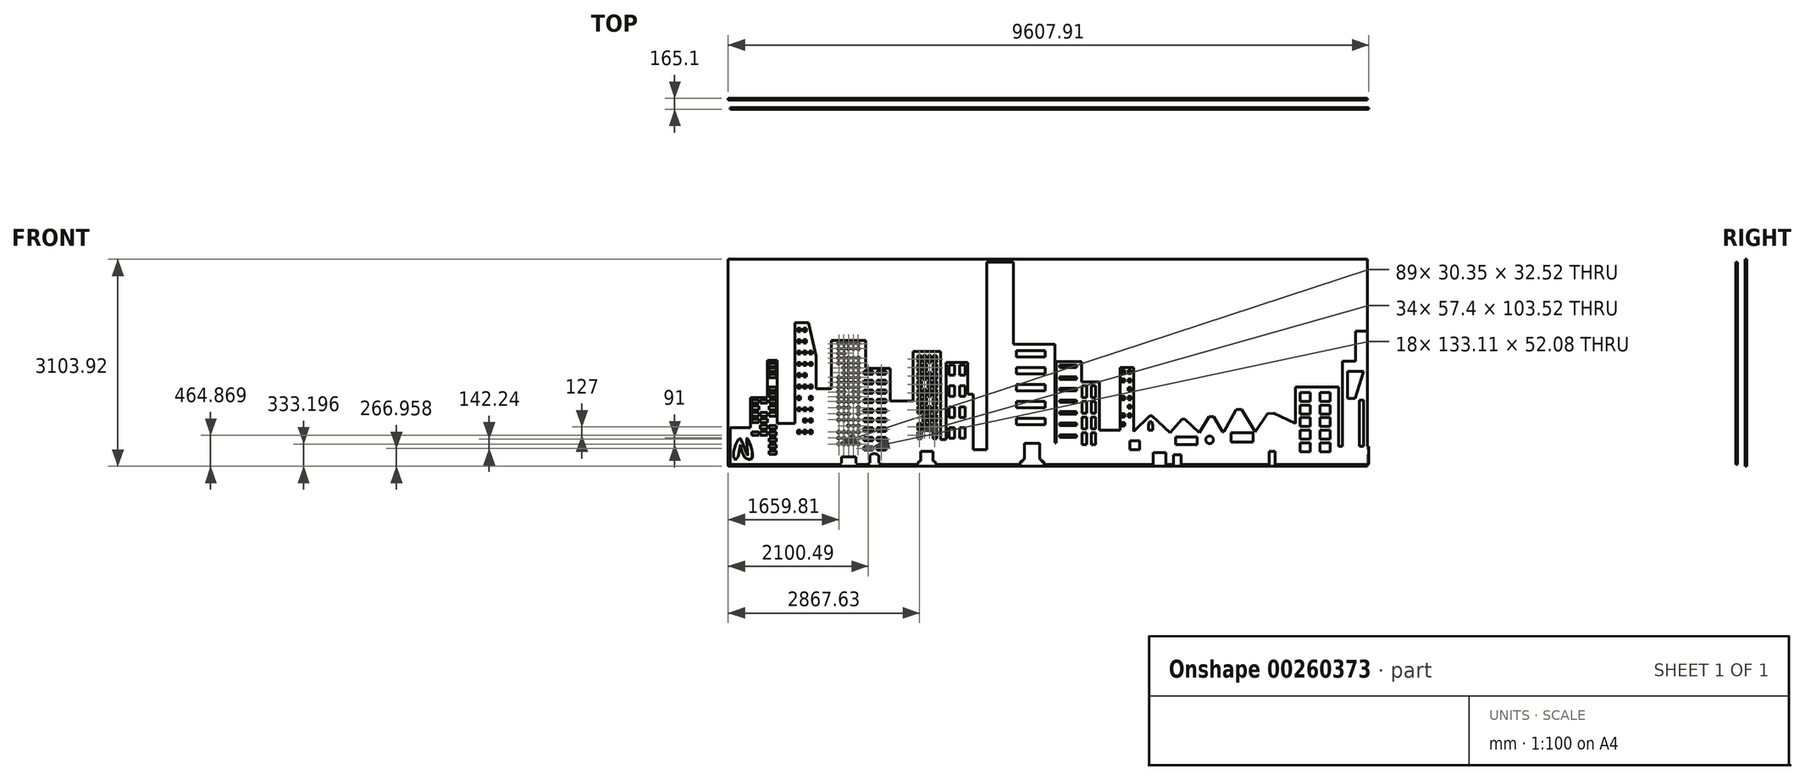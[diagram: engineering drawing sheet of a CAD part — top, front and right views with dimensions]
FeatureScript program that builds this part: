
annotation { "Feature Type Name" : "Feature", "Feature Type Description" : "" }
export const myFeature = defineFeature(function(context is Context, id is Id, definition is map)
    precondition{}
    {
        {
            var Q0;
            Q0=qCreatedBy(makeId("Front.planeOp"),FACE);
            var sketch = newSketch(context, id + "F0", { "sketchPlane" : qUnion([Q0])});
            skLineSegment(sketch, "E0.top", {"start": v(-4050, -823.15) * mm, "end": v(200, -823.15) * mm});
            skLineSegment(sketch, "E0.right", {"start": v(5530, -547.29) * mm, "end": v(5530, -823.15) * mm});
            skLineSegment(sketch, "E1", {"start": v(0, 692.97) * mm, "end": v(0, 1385.94) * mm, "construction": true});
            skLineSegment(sketch, "E2.bottom", {"start": v(-200, -823.15) * mm, "end": v(200, -823.15) * mm});
            skLineSegment(sketch, "E2.top", {"start": v(-200, 2209.1) * mm, "end": v(200, 2209.1) * mm});
            skPoint(sketch, "E2.middle", {"position": v(0, 692.97) * mm});
            skLineSegment(sketch, "E3", {"start": v(-4050, -267.9) * mm, "end": v(-3744.51, -267.9) * mm});
            skLineSegment(sketch, "E4", {"start": v(-3744.51, -267.9) * mm, "end": v(-3744.51, 182.25) * mm});
            skLineSegment(sketch, "E5", {"start": v(-3744.51, 182.25) * mm, "end": v(-3487.34, 182.25) * mm});
            skLineSegment(sketch, "E6", {"start": v(-2077.34, -479.2) * mm, "end": v(-2077.34, 617.88) * mm});
            skLineSegment(sketch, "E7", {"start": v(-2077.34, 617.88) * mm, "end": v(-1645.57, 617.88) * mm});
            skLineSegment(sketch, "E8", {"start": v(-1645.57, 617.88) * mm, "end": v(-1645.57, 127.13) * mm});
            skLineSegment(sketch, "E9", {"start": v(-1645.57, 127.13) * mm, "end": v(-1305.66, 127.13) * mm});
            skLineSegment(sketch, "E10", {"start": v(-1305.66, 127.13) * mm, "end": v(-1305.66, 871.24) * mm});
            skLineSegment(sketch, "E11", {"start": v(-1305.66, 871.24) * mm, "end": v(-892.27, 871.24) * mm});
            skLineSegment(sketch, "E12", {"start": v(-892.27, 871.24) * mm, "end": v(-892.27, -451.63) * mm});
            skLineSegment(sketch, "E13", {"start": v(-892.27, -451.63) * mm, "end": v(-812.32, -451.63) * mm});
            skLineSegment(sketch, "E14", {"start": v(-484.42, 228.18) * mm, "end": v(-402.68, 228.18) * mm});
            skLineSegment(sketch, "E15", {"start": v(-402.68, 228.18) * mm, "end": v(-402.68, -598.62) * mm});
            skLineSegment(sketch, "E16", {"start": v(-402.68, -598.62) * mm, "end": v(-200, -598.62) * mm});
            skLineSegment(sketch, "E17.right", {"start": v(677.5, 629.06) * mm, "end": v(677.5, 534.62) * mm});
            skLineSegment(sketch, "E18", {"start": v(-812.32, 709.79) * mm, "end": v(-484.42, 709.79) * mm});
            skLineSegment(sketch, "E19", {"start": v(-484.42, 709.79) * mm, "end": v(-484.42, 228.18) * mm});
            skLineSegment(sketch, "E20", {"start": v(840.6, 718.46) * mm, "end": v(1218.73, 718.46) * mm});
            skLineSegment(sketch, "E21", {"start": v(1218.73, 718.46) * mm, "end": v(1218.73, 413.8) * mm});
            skLineSegment(sketch, "E22", {"start": v(2725.07, -144.63) * mm, "end": v(2549.54, -345.87) * mm});
            skLineSegment(sketch, "E23", {"start": v(2768.68, -144.63) * mm, "end": v(2987.94, -346.12) * mm});
            skLineSegment(sketch, "E24", {"start": v(2486.2, -646.21) * mm, "end": v(2486.2, -823.15) * mm});
            skLineSegment(sketch, "E25", {"start": v(1218.73, 413.8) * mm, "end": v(1485.88, 413.8) * mm});
            skLineSegment(sketch, "E26", {"start": v(1485.88, 413.8) * mm, "end": v(1485.88, -308) * mm});
            skLineSegment(sketch, "E27", {"start": v(1485.88, -308) * mm, "end": v(1796.4, -308) * mm});
            skLineSegment(sketch, "E28", {"start": v(1796.4, -308) * mm, "end": v(1796.4, 630.35) * mm});
            skLineSegment(sketch, "E29", {"start": v(1796.4, 630.35) * mm, "end": v(2001.46, 630.35) * mm});
            skLineSegment(sketch, "E30", {"start": v(2001.46, 630.35) * mm, "end": v(2001.46, -329.92) * mm});
            skPoint(sketch, "E31.orphan", {"position": v(2356.52, -567.16) * mm});
            skLineSegment(sketch, "E32", {"start": v(2001.46, -329.92) * mm, "end": v(2244.2, -90.17) * mm});
            skLineSegment(sketch, "E33", {"start": v(2923.06, 0) * mm, "end": v(2923.06, 0) * mm});
            skLineSegment(sketch, "E34.2.0.0", {"start": v(-2433.27, 103.48) * mm, "end": v(-2402.92, 103.48) * mm});
            skLineSegment(sketch, "E34.2.0.1", {"start": v(-2402.92, 136) * mm, "end": v(-2402.92, 103.48) * mm});
            skLineSegment(sketch, "E34.2.0.2", {"start": v(-2433.27, 136) * mm, "end": v(-2402.92, 136) * mm});
            skLineSegment(sketch, "E34.2.0.3", {"start": v(-2433.27, 136) * mm, "end": v(-2433.27, 103.48) * mm});
            skLineSegment(sketch, "E35.bottom", {"start": v(-2043.97, 580.46) * mm, "end": v(-1910.86, 580.46) * mm});
            skLineSegment(sketch, "E35.top", {"start": v(-2043.97, 528.38) * mm, "end": v(-1910.86, 528.38) * mm});
            skLineSegment(sketch, "E35.left", {"start": v(-2043.97, 580.46) * mm, "end": v(-2043.97, 528.38) * mm});
            skLineSegment(sketch, "E35.right", {"start": v(-1910.86, 580.46) * mm, "end": v(-1910.86, 528.38) * mm});
            skLineSegment(sketch, "E36.0.1.0", {"start": v(-2043.97, 438.22) * mm, "end": v(-1910.86, 438.22) * mm});
            skLineSegment(sketch, "E36.0.1.1", {"start": v(-2043.97, 386.14) * mm, "end": v(-1910.86, 386.14) * mm});
            skLineSegment(sketch, "E36.0.1.2", {"start": v(-1910.86, 438.22) * mm, "end": v(-1910.86, 386.14) * mm});
            skLineSegment(sketch, "E36.0.1.3", {"start": v(-2043.97, 438.22) * mm, "end": v(-2043.97, 386.14) * mm});
            skLineSegment(sketch, "E36.0.2.0", {"start": v(-2043.97, 295.98) * mm, "end": v(-1910.86, 295.98) * mm});
            skLineSegment(sketch, "E36.0.2.1", {"start": v(-2043.97, 243.9) * mm, "end": v(-1910.86, 243.9) * mm});
            skLineSegment(sketch, "E36.0.2.2", {"start": v(-1910.86, 295.98) * mm, "end": v(-1910.86, 243.9) * mm});
            skLineSegment(sketch, "E36.0.2.3", {"start": v(-2043.97, 295.98) * mm, "end": v(-2043.97, 243.9) * mm});
            skLineSegment(sketch, "E36.0.3.0", {"start": v(-2043.97, 153.74) * mm, "end": v(-1910.86, 153.74) * mm});
            skLineSegment(sketch, "E36.0.3.1", {"start": v(-2043.97, 101.66) * mm, "end": v(-1910.86, 101.66) * mm});
            skLineSegment(sketch, "E36.0.3.2", {"start": v(-1910.86, 153.74) * mm, "end": v(-1910.86, 101.66) * mm});
            skLineSegment(sketch, "E36.0.3.3", {"start": v(-2043.97, 153.74) * mm, "end": v(-2043.97, 101.66) * mm});
            skLineSegment(sketch, "E36.0.4.0", {"start": v(-2043.97, 11.5) * mm, "end": v(-1910.86, 11.5) * mm});
            skLineSegment(sketch, "E36.0.4.1", {"start": v(-2043.97, -40.58) * mm, "end": v(-1910.86, -40.58) * mm});
            skLineSegment(sketch, "E36.0.4.2", {"start": v(-1910.86, 11.5) * mm, "end": v(-1910.86, -40.58) * mm});
            skLineSegment(sketch, "E36.0.4.3", {"start": v(-2043.97, 11.5) * mm, "end": v(-2043.97, -40.58) * mm});
            skLineSegment(sketch, "E36.0.5.0", {"start": v(-2043.97, -130.74) * mm, "end": v(-1910.86, -130.74) * mm});
            skLineSegment(sketch, "E36.0.5.1", {"start": v(-2043.97, -182.82) * mm, "end": v(-1910.86, -182.82) * mm});
            skLineSegment(sketch, "E36.0.5.2", {"start": v(-1910.86, -130.74) * mm, "end": v(-1910.86, -182.82) * mm});
            skLineSegment(sketch, "E36.0.5.3", {"start": v(-2043.97, -130.74) * mm, "end": v(-2043.97, -182.82) * mm});
            skLineSegment(sketch, "E36.0.6.0", {"start": v(-2043.97, -272.98) * mm, "end": v(-1910.86, -272.98) * mm});
            skLineSegment(sketch, "E36.0.6.1", {"start": v(-2043.97, -325.06) * mm, "end": v(-1910.86, -325.06) * mm});
            skLineSegment(sketch, "E36.0.6.2", {"start": v(-1910.86, -272.98) * mm, "end": v(-1910.86, -325.06) * mm});
            skLineSegment(sketch, "E36.0.6.3", {"start": v(-2043.97, -272.98) * mm, "end": v(-2043.97, -325.06) * mm});
            skLineSegment(sketch, "E36.0.7.0", {"start": v(-2043.97, -415.22) * mm, "end": v(-1910.86, -415.22) * mm});
            skLineSegment(sketch, "E36.0.7.1", {"start": v(-2043.97, -467.3) * mm, "end": v(-1910.86, -467.3) * mm});
            skLineSegment(sketch, "E36.0.7.2", {"start": v(-1910.86, -415.22) * mm, "end": v(-1910.86, -467.3) * mm});
            skLineSegment(sketch, "E36.0.7.3", {"start": v(-2043.97, -415.22) * mm, "end": v(-2043.97, -467.3) * mm});
            skLineSegment(sketch, "E36.0.8.0", {"start": v(-2043.97, -557.46) * mm, "end": v(-1910.86, -557.46) * mm});
            skLineSegment(sketch, "E36.0.8.1", {"start": v(-2043.97, -609.54) * mm, "end": v(-1910.86, -609.54) * mm});
            skLineSegment(sketch, "E36.0.8.2", {"start": v(-1910.86, -557.46) * mm, "end": v(-1910.86, -609.54) * mm});
            skLineSegment(sketch, "E36.0.8.3", {"start": v(-2043.97, -557.46) * mm, "end": v(-2043.97, -609.54) * mm});
            skLineSegment(sketch, "E36.1.0.0", {"start": v(-1845.85, 580.46) * mm, "end": v(-1712.74, 580.46) * mm});
            skLineSegment(sketch, "E36.1.0.1", {"start": v(-1845.85, 528.38) * mm, "end": v(-1712.74, 528.38) * mm});
            skLineSegment(sketch, "E36.1.0.2", {"start": v(-1712.74, 580.46) * mm, "end": v(-1712.74, 528.38) * mm});
            skLineSegment(sketch, "E36.1.0.3", {"start": v(-1845.85, 580.46) * mm, "end": v(-1845.85, 528.38) * mm});
            skLineSegment(sketch, "E36.1.1.0", {"start": v(-1845.85, 438.22) * mm, "end": v(-1712.74, 438.22) * mm});
            skLineSegment(sketch, "E36.1.1.1", {"start": v(-1845.85, 386.14) * mm, "end": v(-1712.74, 386.14) * mm});
            skLineSegment(sketch, "E36.1.1.2", {"start": v(-1712.74, 438.22) * mm, "end": v(-1712.74, 386.14) * mm});
            skLineSegment(sketch, "E36.1.1.3", {"start": v(-1845.85, 438.22) * mm, "end": v(-1845.85, 386.14) * mm});
            skLineSegment(sketch, "E36.1.2.0", {"start": v(-1845.85, 295.98) * mm, "end": v(-1712.74, 295.98) * mm});
            skLineSegment(sketch, "E36.1.2.1", {"start": v(-1845.85, 243.9) * mm, "end": v(-1712.74, 243.9) * mm});
            skLineSegment(sketch, "E36.1.2.2", {"start": v(-1712.74, 295.98) * mm, "end": v(-1712.74, 243.9) * mm});
            skLineSegment(sketch, "E36.1.2.3", {"start": v(-1845.85, 295.98) * mm, "end": v(-1845.85, 243.9) * mm});
            skLineSegment(sketch, "E36.1.3.0", {"start": v(-1845.85, 153.74) * mm, "end": v(-1712.74, 153.74) * mm});
            skLineSegment(sketch, "E36.1.3.1", {"start": v(-1845.85, 101.66) * mm, "end": v(-1712.74, 101.66) * mm});
            skLineSegment(sketch, "E36.1.3.2", {"start": v(-1712.74, 153.74) * mm, "end": v(-1712.74, 101.66) * mm});
            skLineSegment(sketch, "E36.1.3.3", {"start": v(-1845.85, 153.74) * mm, "end": v(-1845.85, 101.66) * mm});
            skLineSegment(sketch, "E36.1.4.0", {"start": v(-1845.85, 11.5) * mm, "end": v(-1712.74, 11.5) * mm});
            skLineSegment(sketch, "E36.1.4.1", {"start": v(-1845.85, -40.58) * mm, "end": v(-1712.74, -40.58) * mm});
            skLineSegment(sketch, "E36.1.4.2", {"start": v(-1712.74, 11.5) * mm, "end": v(-1712.74, -40.58) * mm});
            skLineSegment(sketch, "E36.1.4.3", {"start": v(-1845.85, 11.5) * mm, "end": v(-1845.85, -40.58) * mm});
            skLineSegment(sketch, "E36.1.5.0", {"start": v(-1845.85, -130.74) * mm, "end": v(-1712.74, -130.74) * mm});
            skLineSegment(sketch, "E36.1.5.1", {"start": v(-1845.85, -182.82) * mm, "end": v(-1712.74, -182.82) * mm});
            skLineSegment(sketch, "E36.1.5.2", {"start": v(-1712.74, -130.74) * mm, "end": v(-1712.74, -182.82) * mm});
            skLineSegment(sketch, "E36.1.5.3", {"start": v(-1845.85, -130.74) * mm, "end": v(-1845.85, -182.82) * mm});
            skLineSegment(sketch, "E36.1.6.0", {"start": v(-1845.85, -272.98) * mm, "end": v(-1712.74, -272.98) * mm});
            skLineSegment(sketch, "E36.1.6.1", {"start": v(-1845.85, -325.06) * mm, "end": v(-1712.74, -325.06) * mm});
            skLineSegment(sketch, "E36.1.6.2", {"start": v(-1712.74, -272.98) * mm, "end": v(-1712.74, -325.06) * mm});
            skLineSegment(sketch, "E36.1.6.3", {"start": v(-1845.85, -272.98) * mm, "end": v(-1845.85, -325.06) * mm});
            skLineSegment(sketch, "E36.1.7.0", {"start": v(-1845.85, -415.22) * mm, "end": v(-1712.74, -415.22) * mm});
            skLineSegment(sketch, "E36.1.7.1", {"start": v(-1845.85, -467.3) * mm, "end": v(-1712.74, -467.3) * mm});
            skLineSegment(sketch, "E36.1.7.2", {"start": v(-1712.74, -415.22) * mm, "end": v(-1712.74, -467.3) * mm});
            skLineSegment(sketch, "E36.1.7.3", {"start": v(-1845.85, -415.22) * mm, "end": v(-1845.85, -467.3) * mm});
            skLineSegment(sketch, "E36.1.8.0", {"start": v(-1845.85, -557.46) * mm, "end": v(-1712.74, -557.46) * mm});
            skLineSegment(sketch, "E36.1.8.1", {"start": v(-1845.85, -609.54) * mm, "end": v(-1712.74, -609.54) * mm});
            skLineSegment(sketch, "E36.1.8.2", {"start": v(-1712.74, -557.46) * mm, "end": v(-1712.74, -609.54) * mm});
            skLineSegment(sketch, "E36.1.8.3", {"start": v(-1845.85, -557.46) * mm, "end": v(-1845.85, -609.54) * mm});
            skLineSegment(sketch, "E36.direction1", {"start": v(-2043.97, 580.46) * mm, "end": v(-1845.85, 580.46) * mm, "construction": true});
            skLineSegment(sketch, "E36.direction2", {"start": v(-2043.97, 580.46) * mm, "end": v(-2043.97, 438.22) * mm, "construction": true});
            skPoint(sketch, "E37.orphan", {"position": v(-2123.27, 617.88) * mm});
            skLineSegment(sketch, "E38", {"start": v(-2016.7, 617.88) * mm, "end": v(-2016.7, 1037.73) * mm});
            skLineSegment(sketch, "E39", {"start": v(-812.32, 709.79) * mm, "end": v(-812.32, -451.63) * mm});
            skLineSegment(sketch, "E40", {"start": v(200, 981.37) * mm, "end": v(819.93, 981.37) * mm});
            skLineSegment(sketch, "E41", {"start": v(819.93, 981.37) * mm, "end": v(819.93, 718.46) * mm});
            skPoint(sketch, "E42.orphan", {"position": v(0, 0) * mm});
            skPoint(sketch, "E43.orphan", {"position": v(819.93, 692.97) * mm});
            skPoint(sketch, "E44.end.orphan", {"position": v(-2100.3, 617.88) * mm});
            skLineSegment(sketch, "E45.bottom", {"start": v(-1238.98, 809.17) * mm, "end": v(-1181.58, 809.17) * mm});
            skLineSegment(sketch, "E45.top", {"start": v(-1238.98, 705.65) * mm, "end": v(-1181.58, 705.65) * mm});
            skLineSegment(sketch, "E45.left", {"start": v(-1238.98, 809.17) * mm, "end": v(-1238.98, 705.65) * mm});
            skLineSegment(sketch, "E45.right", {"start": v(-1181.58, 809.17) * mm, "end": v(-1181.58, 705.65) * mm});
            skLineSegment(sketch, "E46.0.1.0", {"start": v(-1238.98, 682.17) * mm, "end": v(-1238.98, 578.65) * mm});
            skLineSegment(sketch, "E46.0.1.1", {"start": v(-1181.58, 682.17) * mm, "end": v(-1181.58, 578.65) * mm});
            skLineSegment(sketch, "E46.0.1.2", {"start": v(-1238.98, 682.17) * mm, "end": v(-1181.58, 682.17) * mm});
            skLineSegment(sketch, "E46.0.1.3", {"start": v(-1238.98, 578.65) * mm, "end": v(-1181.58, 578.65) * mm});
            skLineSegment(sketch, "E46.0.2.0", {"start": v(-1238.98, 555.17) * mm, "end": v(-1238.98, 451.65) * mm});
            skLineSegment(sketch, "E46.0.2.1", {"start": v(-1181.58, 555.17) * mm, "end": v(-1181.58, 451.65) * mm});
            skLineSegment(sketch, "E46.0.2.2", {"start": v(-1238.98, 555.17) * mm, "end": v(-1181.58, 555.17) * mm});
            skLineSegment(sketch, "E46.0.2.3", {"start": v(-1238.98, 451.65) * mm, "end": v(-1181.58, 451.65) * mm});
            skLineSegment(sketch, "E46.0.3.0", {"start": v(-1238.98, 428.17) * mm, "end": v(-1238.98, 324.65) * mm});
            skLineSegment(sketch, "E46.0.3.1", {"start": v(-1181.58, 428.17) * mm, "end": v(-1181.58, 324.65) * mm});
            skLineSegment(sketch, "E46.0.3.2", {"start": v(-1238.98, 428.17) * mm, "end": v(-1181.58, 428.17) * mm});
            skLineSegment(sketch, "E46.0.3.3", {"start": v(-1238.98, 324.65) * mm, "end": v(-1181.58, 324.65) * mm});
            skLineSegment(sketch, "E46.0.4.0", {"start": v(-1238.98, 301.17) * mm, "end": v(-1238.98, 197.65) * mm});
            skLineSegment(sketch, "E46.0.4.1", {"start": v(-1181.58, 301.17) * mm, "end": v(-1181.58, 197.65) * mm});
            skLineSegment(sketch, "E46.0.4.2", {"start": v(-1238.98, 301.17) * mm, "end": v(-1181.58, 301.17) * mm});
            skLineSegment(sketch, "E46.0.4.3", {"start": v(-1238.98, 197.65) * mm, "end": v(-1181.58, 197.65) * mm});
            skLineSegment(sketch, "E46.0.5.0", {"start": v(-1238.98, 174.17) * mm, "end": v(-1238.98, 70.65) * mm});
            skLineSegment(sketch, "E46.0.5.1", {"start": v(-1181.58, 174.17) * mm, "end": v(-1181.58, 70.65) * mm});
            skLineSegment(sketch, "E46.0.5.2", {"start": v(-1238.98, 174.17) * mm, "end": v(-1181.58, 174.17) * mm});
            skLineSegment(sketch, "E46.0.5.3", {"start": v(-1238.98, 70.65) * mm, "end": v(-1181.58, 70.65) * mm});
            skLineSegment(sketch, "E46.0.6.0", {"start": v(-1238.98, 47.17) * mm, "end": v(-1238.98, -56.35) * mm});
            skLineSegment(sketch, "E46.0.6.1", {"start": v(-1181.58, 47.17) * mm, "end": v(-1181.58, -56.35) * mm});
            skLineSegment(sketch, "E46.0.6.2", {"start": v(-1238.98, 47.17) * mm, "end": v(-1181.58, 47.17) * mm});
            skLineSegment(sketch, "E46.0.6.3", {"start": v(-1238.98, -56.35) * mm, "end": v(-1181.58, -56.35) * mm});
            skLineSegment(sketch, "E46.0.8.0", {"start": v(-1238.98, -206.83) * mm, "end": v(-1238.98, -310.35) * mm});
            skLineSegment(sketch, "E46.0.8.1", {"start": v(-1181.58, -206.83) * mm, "end": v(-1181.58, -310.35) * mm});
            skLineSegment(sketch, "E46.0.8.2", {"start": v(-1238.98, -206.83) * mm, "end": v(-1181.58, -206.83) * mm});
            skLineSegment(sketch, "E46.0.8.3", {"start": v(-1238.98, -310.35) * mm, "end": v(-1181.58, -310.35) * mm});
            skLineSegment(sketch, "E46.0.9.0", {"start": v(-1238.98, -333.83) * mm, "end": v(-1238.98, -437.35) * mm});
            skLineSegment(sketch, "E46.0.9.1", {"start": v(-1181.58, -333.83) * mm, "end": v(-1181.58, -437.35) * mm});
            skLineSegment(sketch, "E46.0.9.2", {"start": v(-1238.98, -333.83) * mm, "end": v(-1181.58, -333.83) * mm});
            skLineSegment(sketch, "E46.0.9.3", {"start": v(-1238.98, -437.35) * mm, "end": v(-1181.58, -437.35) * mm});
            skLineSegment(sketch, "E46.1.0.0", {"start": v(-1162.78, 809.17) * mm, "end": v(-1162.78, 705.65) * mm});
            skLineSegment(sketch, "E46.1.0.1", {"start": v(-1105.38, 809.17) * mm, "end": v(-1105.38, 705.65) * mm});
            skLineSegment(sketch, "E46.1.0.2", {"start": v(-1162.78, 809.17) * mm, "end": v(-1105.38, 809.17) * mm});
            skLineSegment(sketch, "E46.1.0.3", {"start": v(-1162.78, 705.65) * mm, "end": v(-1105.38, 705.65) * mm});
            skLineSegment(sketch, "E46.1.1.0", {"start": v(-1162.78, 682.17) * mm, "end": v(-1162.78, 578.65) * mm});
            skLineSegment(sketch, "E46.1.1.1", {"start": v(-1105.38, 682.17) * mm, "end": v(-1105.38, 578.65) * mm});
            skLineSegment(sketch, "E46.1.1.2", {"start": v(-1162.78, 682.17) * mm, "end": v(-1105.38, 682.17) * mm});
            skLineSegment(sketch, "E46.1.1.3", {"start": v(-1162.78, 578.65) * mm, "end": v(-1105.38, 578.65) * mm});
            skLineSegment(sketch, "E46.1.2.0", {"start": v(-1162.78, 555.17) * mm, "end": v(-1162.78, 451.65) * mm});
            skLineSegment(sketch, "E46.1.2.1", {"start": v(-1105.38, 555.17) * mm, "end": v(-1105.38, 451.65) * mm});
            skLineSegment(sketch, "E46.1.2.2", {"start": v(-1162.78, 555.17) * mm, "end": v(-1105.38, 555.17) * mm});
            skLineSegment(sketch, "E46.1.2.3", {"start": v(-1162.78, 451.65) * mm, "end": v(-1105.38, 451.65) * mm});
            skLineSegment(sketch, "E46.1.4.0", {"start": v(-1162.78, 301.17) * mm, "end": v(-1162.78, 197.65) * mm});
            skLineSegment(sketch, "E46.1.4.1", {"start": v(-1105.38, 301.17) * mm, "end": v(-1105.38, 197.65) * mm});
            skLineSegment(sketch, "E46.1.4.2", {"start": v(-1162.78, 301.17) * mm, "end": v(-1105.38, 301.17) * mm});
            skLineSegment(sketch, "E46.1.4.3", {"start": v(-1162.78, 197.65) * mm, "end": v(-1105.38, 197.65) * mm});
            skLineSegment(sketch, "E46.1.5.0", {"start": v(-1162.78, 174.17) * mm, "end": v(-1162.78, 70.65) * mm});
            skLineSegment(sketch, "E46.1.5.1", {"start": v(-1105.38, 174.17) * mm, "end": v(-1105.38, 70.65) * mm});
            skLineSegment(sketch, "E46.1.5.2", {"start": v(-1162.78, 174.17) * mm, "end": v(-1105.38, 174.17) * mm});
            skLineSegment(sketch, "E46.1.5.3", {"start": v(-1162.78, 70.65) * mm, "end": v(-1105.38, 70.65) * mm});
            skLineSegment(sketch, "E46.1.6.0", {"start": v(-1162.78, 47.17) * mm, "end": v(-1162.78, -56.35) * mm});
            skLineSegment(sketch, "E46.1.6.1", {"start": v(-1105.38, 47.17) * mm, "end": v(-1105.38, -56.35) * mm});
            skLineSegment(sketch, "E46.1.6.2", {"start": v(-1162.78, 47.17) * mm, "end": v(-1105.38, 47.17) * mm});
            skLineSegment(sketch, "E46.1.6.3", {"start": v(-1162.78, -56.35) * mm, "end": v(-1105.38, -56.35) * mm});
            skLineSegment(sketch, "E46.1.7.0", {"start": v(-1162.78, -79.83) * mm, "end": v(-1162.78, -183.35) * mm});
            skLineSegment(sketch, "E46.1.7.1", {"start": v(-1105.38, -79.83) * mm, "end": v(-1105.38, -183.35) * mm});
            skLineSegment(sketch, "E46.1.7.2", {"start": v(-1162.78, -79.83) * mm, "end": v(-1105.38, -79.83) * mm});
            skLineSegment(sketch, "E46.1.7.3", {"start": v(-1162.78, -183.35) * mm, "end": v(-1105.38, -183.35) * mm});
            skLineSegment(sketch, "E46.1.8.0", {"start": v(-1162.78, -206.83) * mm, "end": v(-1162.78, -310.35) * mm});
            skLineSegment(sketch, "E46.1.8.1", {"start": v(-1105.38, -206.83) * mm, "end": v(-1105.38, -310.35) * mm});
            skLineSegment(sketch, "E46.1.8.2", {"start": v(-1162.78, -206.83) * mm, "end": v(-1105.38, -206.83) * mm});
            skLineSegment(sketch, "E46.1.8.3", {"start": v(-1162.78, -310.35) * mm, "end": v(-1105.38, -310.35) * mm});
            skLineSegment(sketch, "E46.2.0.0", {"start": v(-1086.58, 809.17) * mm, "end": v(-1086.58, 705.65) * mm});
            skLineSegment(sketch, "E46.2.0.1", {"start": v(-1029.18, 809.17) * mm, "end": v(-1029.18, 705.65) * mm});
            skLineSegment(sketch, "E46.2.0.2", {"start": v(-1086.58, 809.17) * mm, "end": v(-1029.18, 809.17) * mm});
            skLineSegment(sketch, "E46.2.0.3", {"start": v(-1086.58, 705.65) * mm, "end": v(-1029.18, 705.65) * mm});
            skLineSegment(sketch, "E46.2.2.0", {"start": v(-1086.58, 555.17) * mm, "end": v(-1086.58, 451.65) * mm});
            skLineSegment(sketch, "E46.2.2.1", {"start": v(-1029.18, 555.17) * mm, "end": v(-1029.18, 451.65) * mm});
            skLineSegment(sketch, "E46.2.2.2", {"start": v(-1086.58, 555.17) * mm, "end": v(-1029.18, 555.17) * mm});
            skLineSegment(sketch, "E46.2.2.3", {"start": v(-1086.58, 451.65) * mm, "end": v(-1029.18, 451.65) * mm});
            skLineSegment(sketch, "E46.2.3.0", {"start": v(-1086.58, 428.17) * mm, "end": v(-1086.58, 324.65) * mm});
            skLineSegment(sketch, "E46.2.3.1", {"start": v(-1029.18, 428.17) * mm, "end": v(-1029.18, 324.65) * mm});
            skLineSegment(sketch, "E46.2.3.2", {"start": v(-1086.58, 428.17) * mm, "end": v(-1029.18, 428.17) * mm});
            skLineSegment(sketch, "E46.2.3.3", {"start": v(-1086.58, 324.65) * mm, "end": v(-1029.18, 324.65) * mm});
            skLineSegment(sketch, "E46.2.4.0", {"start": v(-1086.58, 301.17) * mm, "end": v(-1086.58, 197.65) * mm});
            skLineSegment(sketch, "E46.2.4.1", {"start": v(-1029.18, 301.17) * mm, "end": v(-1029.18, 197.65) * mm});
            skLineSegment(sketch, "E46.2.4.2", {"start": v(-1086.58, 301.17) * mm, "end": v(-1029.18, 301.17) * mm});
            skLineSegment(sketch, "E46.2.4.3", {"start": v(-1086.58, 197.65) * mm, "end": v(-1029.18, 197.65) * mm});
            skLineSegment(sketch, "E46.2.6.0", {"start": v(-1086.58, 47.17) * mm, "end": v(-1086.58, -56.35) * mm});
            skLineSegment(sketch, "E46.2.6.1", {"start": v(-1029.18, 47.17) * mm, "end": v(-1029.18, -56.35) * mm});
            skLineSegment(sketch, "E46.2.6.2", {"start": v(-1086.58, 47.17) * mm, "end": v(-1029.18, 47.17) * mm});
            skLineSegment(sketch, "E46.2.6.3", {"start": v(-1086.58, -56.35) * mm, "end": v(-1029.18, -56.35) * mm});
            skLineSegment(sketch, "E46.2.7.0", {"start": v(-1086.58, -79.83) * mm, "end": v(-1086.58, -183.35) * mm});
            skLineSegment(sketch, "E46.2.7.1", {"start": v(-1029.18, -79.83) * mm, "end": v(-1029.18, -183.35) * mm});
            skLineSegment(sketch, "E46.2.7.2", {"start": v(-1086.58, -79.83) * mm, "end": v(-1029.18, -79.83) * mm});
            skLineSegment(sketch, "E46.2.7.3", {"start": v(-1086.58, -183.35) * mm, "end": v(-1029.18, -183.35) * mm});
            skLineSegment(sketch, "E46.2.8.0", {"start": v(-1086.58, -206.83) * mm, "end": v(-1086.58, -310.35) * mm});
            skLineSegment(sketch, "E46.2.8.1", {"start": v(-1029.18, -206.83) * mm, "end": v(-1029.18, -310.35) * mm});
            skLineSegment(sketch, "E46.2.8.2", {"start": v(-1086.58, -206.83) * mm, "end": v(-1029.18, -206.83) * mm});
            skLineSegment(sketch, "E46.2.8.3", {"start": v(-1086.58, -310.35) * mm, "end": v(-1029.18, -310.35) * mm});
            skLineSegment(sketch, "E46.3.0.0", {"start": v(-1010.38, 809.17) * mm, "end": v(-1010.38, 705.65) * mm});
            skLineSegment(sketch, "E46.3.0.1", {"start": v(-952.98, 809.17) * mm, "end": v(-952.98, 705.65) * mm});
            skLineSegment(sketch, "E46.3.0.2", {"start": v(-1010.38, 809.17) * mm, "end": v(-952.98, 809.17) * mm});
            skLineSegment(sketch, "E46.3.0.3", {"start": v(-1010.38, 705.65) * mm, "end": v(-952.98, 705.65) * mm});
            skLineSegment(sketch, "E46.3.1.0", {"start": v(-1010.38, 682.17) * mm, "end": v(-1010.38, 578.65) * mm});
            skLineSegment(sketch, "E46.3.1.1", {"start": v(-952.98, 682.17) * mm, "end": v(-952.98, 578.65) * mm});
            skLineSegment(sketch, "E46.3.1.2", {"start": v(-1010.38, 682.17) * mm, "end": v(-952.98, 682.17) * mm});
            skLineSegment(sketch, "E46.3.1.3", {"start": v(-1010.38, 578.65) * mm, "end": v(-952.98, 578.65) * mm});
            skLineSegment(sketch, "E46.3.2.0", {"start": v(-1010.38, 555.17) * mm, "end": v(-1010.38, 451.65) * mm});
            skLineSegment(sketch, "E46.3.2.1", {"start": v(-952.98, 555.17) * mm, "end": v(-952.98, 451.65) * mm});
            skLineSegment(sketch, "E46.3.2.2", {"start": v(-1010.38, 555.17) * mm, "end": v(-952.98, 555.17) * mm});
            skLineSegment(sketch, "E46.3.2.3", {"start": v(-1010.38, 451.65) * mm, "end": v(-952.98, 451.65) * mm});
            skLineSegment(sketch, "E46.3.3.0", {"start": v(-1010.38, 428.17) * mm, "end": v(-1010.38, 324.65) * mm});
            skLineSegment(sketch, "E46.3.3.1", {"start": v(-952.98, 428.17) * mm, "end": v(-952.98, 324.65) * mm});
            skLineSegment(sketch, "E46.3.3.2", {"start": v(-1010.38, 428.17) * mm, "end": v(-952.98, 428.17) * mm});
            skLineSegment(sketch, "E46.3.3.3", {"start": v(-1010.38, 324.65) * mm, "end": v(-952.98, 324.65) * mm});
            skLineSegment(sketch, "E46.3.4.0", {"start": v(-1010.38, 301.17) * mm, "end": v(-1010.38, 197.65) * mm});
            skLineSegment(sketch, "E46.3.4.1", {"start": v(-952.98, 301.17) * mm, "end": v(-952.98, 197.65) * mm});
            skLineSegment(sketch, "E46.3.4.2", {"start": v(-1010.38, 301.17) * mm, "end": v(-952.98, 301.17) * mm});
            skLineSegment(sketch, "E46.3.4.3", {"start": v(-1010.38, 197.65) * mm, "end": v(-952.98, 197.65) * mm});
            skLineSegment(sketch, "E46.3.5.0", {"start": v(-1010.38, 174.17) * mm, "end": v(-1010.38, 70.65) * mm});
            skLineSegment(sketch, "E46.3.5.1", {"start": v(-952.98, 174.17) * mm, "end": v(-952.98, 70.65) * mm});
            skLineSegment(sketch, "E46.3.5.2", {"start": v(-1010.38, 174.17) * mm, "end": v(-952.98, 174.17) * mm});
            skLineSegment(sketch, "E46.3.5.3", {"start": v(-1010.38, 70.65) * mm, "end": v(-952.98, 70.65) * mm});
            skLineSegment(sketch, "E46.3.6.0", {"start": v(-1010.38, 47.17) * mm, "end": v(-1010.38, -56.35) * mm});
            skLineSegment(sketch, "E46.3.6.1", {"start": v(-952.98, 47.17) * mm, "end": v(-952.98, -56.35) * mm});
            skLineSegment(sketch, "E46.3.6.2", {"start": v(-1010.38, 47.17) * mm, "end": v(-952.98, 47.17) * mm});
            skLineSegment(sketch, "E46.3.6.3", {"start": v(-1010.38, -56.35) * mm, "end": v(-952.98, -56.35) * mm});
            skLineSegment(sketch, "E46.3.7.0", {"start": v(-1010.38, -79.83) * mm, "end": v(-1010.38, -183.35) * mm});
            skLineSegment(sketch, "E46.3.7.1", {"start": v(-952.98, -79.83) * mm, "end": v(-952.98, -183.35) * mm});
            skLineSegment(sketch, "E46.3.7.2", {"start": v(-1010.38, -79.83) * mm, "end": v(-952.98, -79.83) * mm});
            skLineSegment(sketch, "E46.3.7.3", {"start": v(-1010.38, -183.35) * mm, "end": v(-952.98, -183.35) * mm});
            skLineSegment(sketch, "E46.3.8.0", {"start": v(-1010.38, -206.83) * mm, "end": v(-1010.38, -310.35) * mm});
            skLineSegment(sketch, "E46.3.8.1", {"start": v(-952.98, -206.83) * mm, "end": v(-952.98, -310.35) * mm});
            skLineSegment(sketch, "E46.3.8.2", {"start": v(-1010.38, -206.83) * mm, "end": v(-952.98, -206.83) * mm});
            skLineSegment(sketch, "E46.3.8.3", {"start": v(-1010.38, -310.35) * mm, "end": v(-952.98, -310.35) * mm});
            skLineSegment(sketch, "E46.3.9.0", {"start": v(-1010.38, -333.83) * mm, "end": v(-1010.38, -437.35) * mm});
            skLineSegment(sketch, "E46.3.9.1", {"start": v(-952.98, -333.83) * mm, "end": v(-952.98, -437.35) * mm});
            skLineSegment(sketch, "E46.3.9.2", {"start": v(-1010.38, -333.83) * mm, "end": v(-952.98, -333.83) * mm});
            skLineSegment(sketch, "E46.3.9.3", {"start": v(-1010.38, -437.35) * mm, "end": v(-952.98, -437.35) * mm});
            skLineSegment(sketch, "E46.direction1", {"start": v(-1238.98, 705.65) * mm, "end": v(-1162.78, 705.65) * mm, "construction": true});
            skLineSegment(sketch, "E46.direction2", {"start": v(-1238.98, 705.65) * mm, "end": v(-1238.98, 578.65) * mm, "construction": true});
            skLineSegment(sketch, "E47.bottom", {"start": v(1943.47, -469.79) * mm, "end": v(2093.34, -469.79) * mm});
            skLineSegment(sketch, "E47.top", {"start": v(1943.47, -603.88) * mm, "end": v(2093.34, -603.88) * mm});
            skLineSegment(sketch, "E47.left", {"start": v(1943.47, -469.79) * mm, "end": v(1943.47, -603.88) * mm});
            skLineSegment(sketch, "E47.right", {"start": v(2093.34, -469.79) * mm, "end": v(2093.34, -603.88) * mm});
            skLineSegment(sketch, "E48.bottom", {"start": v(2601.85, -823.15) * mm, "end": v(2712.28, -823.15) * mm});
            skLineSegment(sketch, "E48.top", {"start": v(2601.85, -680.13) * mm, "end": v(2712.28, -680.13) * mm});
            skLineSegment(sketch, "E48.left", {"start": v(2601.85, -823.15) * mm, "end": v(2601.85, -680.13) * mm});
            skLineSegment(sketch, "E48.right", {"start": v(2712.28, -823.15) * mm, "end": v(2712.28, -680.13) * mm});
            skCircle(sketch, "E49", {"center": v(3141.04, -452.93) * mm, "radius": 57.13 * mm});
            skLineSegment(sketch, "E50.bottom", {"start": v(3464.56, -345.03) * mm, "end": v(3791.78, -345.03) * mm});
            skLineSegment(sketch, "E50.top", {"start": v(3464.56, -486.32) * mm, "end": v(3791.78, -486.32) * mm});
            skLineSegment(sketch, "E50.left", {"start": v(3464.56, -345.03) * mm, "end": v(3464.56, -486.32) * mm});
            skLineSegment(sketch, "E50.right", {"start": v(3791.78, -345.03) * mm, "end": v(3791.78, -486.32) * mm});
            skLineSegment(sketch, "E51.bottom", {"start": v(2292, -646.21) * mm, "end": v(2486.2, -646.21) * mm});
            skLineSegment(sketch, "E51.top", {"start": v(2292, -823.15) * mm, "end": v(2486.2, -823.15) * mm});
            skLineSegment(sketch, "E51.left", {"start": v(2292, -646.21) * mm, "end": v(2292, -823.15) * mm});
            skFitSpline(sketch, "E52", {"points": [v(-3999, -718.57) * mm, v(-3923.83, -444.41) * mm, v(-3888.45, -444.41) * mm, v(-3786.75, -683.2) * mm, v(-3800.02, -435.57) * mm, v(-3773.48, -457.68) * mm, v(-3724.84, -736.26) * mm, v(-3848.66, -692.04) * mm, v(-3897.3, -528.43) * mm, v(-3950.36, -745.1) * mm, v(-3999, -718.57) * mm]});
            skLineSegment(sketch, "E53.0.1.0", {"start": v(246.5, 629.06) * mm, "end": v(677.5, 629.06) * mm});
            skLineSegment(sketch, "E53.0.1.2", {"start": v(246.5, 534.62) * mm, "end": v(677.5, 534.62) * mm});
            skLineSegment(sketch, "E53.0.2.0", {"start": v(246.5, 375.06) * mm, "end": v(677.5, 375.06) * mm});
            skLineSegment(sketch, "E53.0.2.2", {"start": v(246.5, 280.62) * mm, "end": v(677.5, 280.62) * mm});
            skLineSegment(sketch, "E53.0.3.0", {"start": v(246.5, 121.06) * mm, "end": v(677.5, 121.06) * mm});
            skLineSegment(sketch, "E53.0.3.2", {"start": v(246.5, 26.62) * mm, "end": v(677.5, 26.62) * mm});
            skLineSegment(sketch, "E53.0.4.0", {"start": v(246.5, -132.94) * mm, "end": v(677.5, -132.94) * mm});
            skLineSegment(sketch, "E53.0.4.2", {"start": v(246.5, -227.38) * mm, "end": v(677.5, -227.38) * mm});
            skLineSegment(sketch, "E54.trimOffspring", {"start": v(677.5, 375.06) * mm, "end": v(677.5, 280.62) * mm});
            skLineSegment(sketch, "E55.trimOffspring", {"start": v(677.5, -132.94) * mm, "end": v(677.5, -227.38) * mm});
            skLineSegment(sketch, "E56.bottom", {"start": v(-766.41, 671.26) * mm, "end": v(-683.53, 671.26) * mm});
            skLineSegment(sketch, "E56.top", {"start": v(-766.41, 514.48) * mm, "end": v(-683.53, 514.48) * mm});
            skLineSegment(sketch, "E56.left", {"start": v(-766.41, 671.26) * mm, "end": v(-766.41, 514.48) * mm});
            skLineSegment(sketch, "E56.right", {"start": v(-683.53, 671.26) * mm, "end": v(-683.53, 514.48) * mm});
            skLineSegment(sketch, "E57.0.1.0", {"start": v(-766.41, 356.3) * mm, "end": v(-683.53, 356.3) * mm});
            skLineSegment(sketch, "E57.0.1.1", {"start": v(-766.41, 356.3) * mm, "end": v(-766.41, 199.52) * mm});
            skLineSegment(sketch, "E57.0.1.2", {"start": v(-683.53, 356.3) * mm, "end": v(-683.53, 199.52) * mm});
            skLineSegment(sketch, "E57.0.1.3", {"start": v(-766.41, 199.52) * mm, "end": v(-683.53, 199.52) * mm});
            skLineSegment(sketch, "E57.0.2.0", {"start": v(-766.41, 41.34) * mm, "end": v(-683.53, 41.34) * mm});
            skLineSegment(sketch, "E57.0.2.1", {"start": v(-766.41, 41.34) * mm, "end": v(-766.41, -115.44) * mm});
            skLineSegment(sketch, "E57.0.2.2", {"start": v(-683.53, 41.34) * mm, "end": v(-683.53, -115.44) * mm});
            skLineSegment(sketch, "E57.0.2.3", {"start": v(-766.41, -115.44) * mm, "end": v(-683.53, -115.44) * mm});
            skLineSegment(sketch, "E57.0.3.0", {"start": v(-766.41, -273.62) * mm, "end": v(-683.53, -273.62) * mm});
            skLineSegment(sketch, "E57.0.3.1", {"start": v(-766.41, -273.62) * mm, "end": v(-766.41, -430.4) * mm});
            skLineSegment(sketch, "E57.0.3.2", {"start": v(-683.53, -273.62) * mm, "end": v(-683.53, -430.4) * mm});
            skLineSegment(sketch, "E57.0.3.3", {"start": v(-766.41, -430.4) * mm, "end": v(-683.53, -430.4) * mm});
            skLineSegment(sketch, "E57.1.0.0", {"start": v(-606.4, 671.26) * mm, "end": v(-523.5, 671.26) * mm});
            skLineSegment(sketch, "E57.1.0.1", {"start": v(-606.4, 671.26) * mm, "end": v(-606.4, 514.48) * mm});
            skLineSegment(sketch, "E57.1.0.2", {"start": v(-523.5, 671.26) * mm, "end": v(-523.5, 514.48) * mm});
            skLineSegment(sketch, "E57.1.0.3", {"start": v(-606.4, 514.48) * mm, "end": v(-523.5, 514.48) * mm});
            skLineSegment(sketch, "E57.1.1.0", {"start": v(-606.4, 356.3) * mm, "end": v(-523.5, 356.3) * mm});
            skLineSegment(sketch, "E57.1.1.1", {"start": v(-606.4, 356.3) * mm, "end": v(-606.4, 199.52) * mm});
            skLineSegment(sketch, "E57.1.1.2", {"start": v(-523.5, 356.3) * mm, "end": v(-523.5, 199.52) * mm});
            skLineSegment(sketch, "E57.1.1.3", {"start": v(-606.4, 199.52) * mm, "end": v(-523.5, 199.52) * mm});
            skLineSegment(sketch, "E57.1.2.0", {"start": v(-606.4, 41.34) * mm, "end": v(-523.5, 41.34) * mm});
            skLineSegment(sketch, "E57.1.2.1", {"start": v(-606.4, 41.34) * mm, "end": v(-606.4, -115.44) * mm});
            skLineSegment(sketch, "E57.1.2.2", {"start": v(-523.5, 41.34) * mm, "end": v(-523.5, -115.44) * mm});
            skLineSegment(sketch, "E57.1.2.3", {"start": v(-606.4, -115.44) * mm, "end": v(-523.5, -115.44) * mm});
            skLineSegment(sketch, "E57.1.3.0", {"start": v(-606.4, -273.62) * mm, "end": v(-523.5, -273.62) * mm});
            skLineSegment(sketch, "E57.1.3.1", {"start": v(-606.4, -273.62) * mm, "end": v(-606.4, -430.4) * mm});
            skLineSegment(sketch, "E57.1.3.2", {"start": v(-523.5, -273.62) * mm, "end": v(-523.5, -430.4) * mm});
            skLineSegment(sketch, "E57.1.3.3", {"start": v(-606.4, -430.4) * mm, "end": v(-523.5, -430.4) * mm});
            skLineSegment(sketch, "E57.direction1", {"start": v(-766.41, 671.26) * mm, "end": v(-606.4, 671.26) * mm, "construction": true});
            skLineSegment(sketch, "E57.direction2", {"start": v(-766.41, 671.26) * mm, "end": v(-766.41, 356.3) * mm, "construction": true});
            skLineSegment(sketch, "E58", {"start": v(677.5, 121.06) * mm, "end": v(677.5, 26.62) * mm});
            skLineSegment(sketch, "E59", {"start": v(677.5, 788.62) * mm, "end": v(677.5, 883.06) * mm});
            skLineSegment(sketch, "E60.0.1.0", {"start": v(-2433.27, 208.38) * mm, "end": v(-2402.92, 208.38) * mm});
            skLineSegment(sketch, "E60.0.1.1", {"start": v(-2433.27, 175.87) * mm, "end": v(-2402.92, 175.87) * mm});
            skLineSegment(sketch, "E60.0.1.2", {"start": v(-2402.92, 208.38) * mm, "end": v(-2402.92, 175.87) * mm});
            skLineSegment(sketch, "E60.0.1.3", {"start": v(-2433.27, 208.38) * mm, "end": v(-2433.27, 175.87) * mm});
            skLineSegment(sketch, "E60.0.2.0", {"start": v(-2433.27, 280.77) * mm, "end": v(-2402.92, 280.77) * mm});
            skLineSegment(sketch, "E60.0.2.1", {"start": v(-2433.27, 248.26) * mm, "end": v(-2402.92, 248.26) * mm});
            skLineSegment(sketch, "E60.0.2.2", {"start": v(-2402.92, 280.77) * mm, "end": v(-2402.92, 248.26) * mm});
            skLineSegment(sketch, "E60.0.2.3", {"start": v(-2433.27, 280.77) * mm, "end": v(-2433.27, 248.26) * mm});
            skLineSegment(sketch, "E60.0.3.0", {"start": v(-2433.27, 353.16) * mm, "end": v(-2402.92, 353.16) * mm});
            skLineSegment(sketch, "E60.0.3.1", {"start": v(-2433.27, 320.65) * mm, "end": v(-2402.92, 320.65) * mm});
            skLineSegment(sketch, "E60.0.3.2", {"start": v(-2402.92, 353.16) * mm, "end": v(-2402.92, 320.65) * mm});
            skLineSegment(sketch, "E60.0.3.3", {"start": v(-2433.27, 353.16) * mm, "end": v(-2433.27, 320.65) * mm});
            skLineSegment(sketch, "E60.0.4.0", {"start": v(-2433.27, 425.55) * mm, "end": v(-2402.92, 425.55) * mm});
            skLineSegment(sketch, "E60.0.4.1", {"start": v(-2433.27, 393.04) * mm, "end": v(-2402.92, 393.04) * mm});
            skLineSegment(sketch, "E60.0.4.2", {"start": v(-2402.92, 425.55) * mm, "end": v(-2402.92, 393.04) * mm});
            skLineSegment(sketch, "E60.0.4.3", {"start": v(-2433.27, 425.55) * mm, "end": v(-2433.27, 393.04) * mm});
            skLineSegment(sketch, "E60.0.5.0", {"start": v(-2433.27, 497.94) * mm, "end": v(-2402.92, 497.94) * mm});
            skLineSegment(sketch, "E60.0.5.1", {"start": v(-2433.27, 465.43) * mm, "end": v(-2402.92, 465.43) * mm});
            skLineSegment(sketch, "E60.0.5.2", {"start": v(-2402.92, 497.94) * mm, "end": v(-2402.92, 465.43) * mm});
            skLineSegment(sketch, "E60.0.5.3", {"start": v(-2433.27, 497.94) * mm, "end": v(-2433.27, 465.43) * mm});
            skLineSegment(sketch, "E60.0.8.0", {"start": v(-2433.27, 715.11) * mm, "end": v(-2402.92, 715.11) * mm});
            skLineSegment(sketch, "E60.0.8.1", {"start": v(-2433.27, 682.6) * mm, "end": v(-2402.92, 682.6) * mm});
            skLineSegment(sketch, "E60.0.8.2", {"start": v(-2402.92, 715.11) * mm, "end": v(-2402.92, 682.6) * mm});
            skLineSegment(sketch, "E60.0.8.3", {"start": v(-2433.27, 715.11) * mm, "end": v(-2433.27, 682.6) * mm});
            skLineSegment(sketch, "E60.0.9.0", {"start": v(-2433.27, 787.5) * mm, "end": v(-2402.92, 787.5) * mm});
            skLineSegment(sketch, "E60.0.9.1", {"start": v(-2433.27, 754.99) * mm, "end": v(-2402.92, 754.99) * mm});
            skLineSegment(sketch, "E60.0.9.2", {"start": v(-2402.92, 787.5) * mm, "end": v(-2402.92, 754.99) * mm});
            skLineSegment(sketch, "E60.0.9.3", {"start": v(-2433.27, 787.5) * mm, "end": v(-2433.27, 754.99) * mm});
            skLineSegment(sketch, "E60.0.10.0", {"start": v(-2433.27, 859.9) * mm, "end": v(-2402.92, 859.9) * mm});
            skLineSegment(sketch, "E60.0.10.1", {"start": v(-2433.27, 827.38) * mm, "end": v(-2402.92, 827.38) * mm});
            skLineSegment(sketch, "E60.0.10.2", {"start": v(-2402.92, 859.9) * mm, "end": v(-2402.92, 827.38) * mm});
            skLineSegment(sketch, "E60.0.10.3", {"start": v(-2433.27, 859.9) * mm, "end": v(-2433.27, 827.38) * mm});
            skLineSegment(sketch, "E60.0.11.0", {"start": v(-2433.27, 932.28) * mm, "end": v(-2402.92, 932.28) * mm});
            skLineSegment(sketch, "E60.0.11.1", {"start": v(-2433.27, 899.77) * mm, "end": v(-2402.92, 899.77) * mm});
            skLineSegment(sketch, "E60.0.11.2", {"start": v(-2402.92, 932.28) * mm, "end": v(-2402.92, 899.77) * mm});
            skLineSegment(sketch, "E60.0.11.3", {"start": v(-2433.27, 932.28) * mm, "end": v(-2433.27, 899.77) * mm});
            skLineSegment(sketch, "E60.0.12.0", {"start": v(-2433.27, 1004.67) * mm, "end": v(-2402.92, 1004.67) * mm});
            skLineSegment(sketch, "E60.0.12.1", {"start": v(-2433.27, 972.16) * mm, "end": v(-2402.92, 972.16) * mm});
            skLineSegment(sketch, "E60.0.12.2", {"start": v(-2402.92, 1004.67) * mm, "end": v(-2402.92, 972.16) * mm});
            skLineSegment(sketch, "E60.0.12.3", {"start": v(-2433.27, 1004.67) * mm, "end": v(-2433.27, 972.16) * mm});
            skLineSegment(sketch, "E60.1.0.0", {"start": v(-2360.88, 136) * mm, "end": v(-2330.53, 136) * mm});
            skLineSegment(sketch, "E60.1.0.1", {"start": v(-2360.88, 103.48) * mm, "end": v(-2330.53, 103.48) * mm});
            skLineSegment(sketch, "E60.1.0.2", {"start": v(-2330.53, 136) * mm, "end": v(-2330.53, 103.48) * mm});
            skLineSegment(sketch, "E60.1.0.3", {"start": v(-2360.88, 136) * mm, "end": v(-2360.88, 103.48) * mm});
            skLineSegment(sketch, "E60.1.1.0", {"start": v(-2360.88, 208.38) * mm, "end": v(-2330.53, 208.38) * mm});
            skLineSegment(sketch, "E60.1.1.1", {"start": v(-2360.88, 175.87) * mm, "end": v(-2330.53, 175.87) * mm});
            skLineSegment(sketch, "E60.1.1.2", {"start": v(-2330.53, 208.38) * mm, "end": v(-2330.53, 175.87) * mm});
            skLineSegment(sketch, "E60.1.1.3", {"start": v(-2360.88, 208.38) * mm, "end": v(-2360.88, 175.87) * mm});
            skLineSegment(sketch, "E60.1.2.0", {"start": v(-2360.88, 280.77) * mm, "end": v(-2330.53, 280.77) * mm});
            skLineSegment(sketch, "E60.1.2.1", {"start": v(-2360.88, 248.26) * mm, "end": v(-2330.53, 248.26) * mm});
            skLineSegment(sketch, "E60.1.2.2", {"start": v(-2330.53, 280.77) * mm, "end": v(-2330.53, 248.26) * mm});
            skLineSegment(sketch, "E60.1.2.3", {"start": v(-2360.88, 280.77) * mm, "end": v(-2360.88, 248.26) * mm});
            skLineSegment(sketch, "E60.1.3.0", {"start": v(-2360.88, 353.16) * mm, "end": v(-2330.53, 353.16) * mm});
            skLineSegment(sketch, "E60.1.3.1", {"start": v(-2360.88, 320.65) * mm, "end": v(-2330.53, 320.65) * mm});
            skLineSegment(sketch, "E60.1.3.2", {"start": v(-2330.53, 353.16) * mm, "end": v(-2330.53, 320.65) * mm});
            skLineSegment(sketch, "E60.1.3.3", {"start": v(-2360.88, 353.16) * mm, "end": v(-2360.88, 320.65) * mm});
            skLineSegment(sketch, "E60.1.4.0", {"start": v(-2360.88, 425.55) * mm, "end": v(-2330.53, 425.55) * mm});
            skLineSegment(sketch, "E60.1.4.1", {"start": v(-2360.88, 393.04) * mm, "end": v(-2330.53, 393.04) * mm});
            skLineSegment(sketch, "E60.1.4.2", {"start": v(-2330.53, 425.55) * mm, "end": v(-2330.53, 393.04) * mm});
            skLineSegment(sketch, "E60.1.4.3", {"start": v(-2360.88, 425.55) * mm, "end": v(-2360.88, 393.04) * mm});
            skLineSegment(sketch, "E60.1.5.0", {"start": v(-2360.88, 497.94) * mm, "end": v(-2330.53, 497.94) * mm});
            skLineSegment(sketch, "E60.1.5.1", {"start": v(-2360.88, 465.43) * mm, "end": v(-2330.53, 465.43) * mm});
            skLineSegment(sketch, "E60.1.5.2", {"start": v(-2330.53, 497.94) * mm, "end": v(-2330.53, 465.43) * mm});
            skLineSegment(sketch, "E60.1.5.3", {"start": v(-2360.88, 497.94) * mm, "end": v(-2360.88, 465.43) * mm});
            skLineSegment(sketch, "E60.1.6.0", {"start": v(-2360.88, 570.33) * mm, "end": v(-2330.53, 570.33) * mm});
            skLineSegment(sketch, "E60.1.6.1", {"start": v(-2360.88, 537.82) * mm, "end": v(-2330.53, 537.82) * mm});
            skLineSegment(sketch, "E60.1.6.2", {"start": v(-2330.53, 570.33) * mm, "end": v(-2330.53, 537.82) * mm});
            skLineSegment(sketch, "E60.1.6.3", {"start": v(-2360.88, 570.33) * mm, "end": v(-2360.88, 537.82) * mm});
            skLineSegment(sketch, "E60.1.7.0", {"start": v(-2360.88, 642.72) * mm, "end": v(-2330.53, 642.72) * mm});
            skLineSegment(sketch, "E60.1.7.1", {"start": v(-2360.88, 610.2) * mm, "end": v(-2330.53, 610.2) * mm});
            skLineSegment(sketch, "E60.1.7.2", {"start": v(-2330.53, 642.72) * mm, "end": v(-2330.53, 610.2) * mm});
            skLineSegment(sketch, "E60.1.7.3", {"start": v(-2360.88, 642.72) * mm, "end": v(-2360.88, 610.2) * mm});
            skLineSegment(sketch, "E60.1.8.0", {"start": v(-2360.88, 715.11) * mm, "end": v(-2330.53, 715.11) * mm});
            skLineSegment(sketch, "E60.1.8.1", {"start": v(-2360.88, 682.6) * mm, "end": v(-2330.53, 682.6) * mm});
            skLineSegment(sketch, "E60.1.8.2", {"start": v(-2330.53, 715.11) * mm, "end": v(-2330.53, 682.6) * mm});
            skLineSegment(sketch, "E60.1.8.3", {"start": v(-2360.88, 715.11) * mm, "end": v(-2360.88, 682.6) * mm});
            skLineSegment(sketch, "E60.1.9.0", {"start": v(-2360.88, 787.5) * mm, "end": v(-2330.53, 787.5) * mm});
            skLineSegment(sketch, "E60.1.9.1", {"start": v(-2360.88, 754.99) * mm, "end": v(-2330.53, 754.99) * mm});
            skLineSegment(sketch, "E60.1.9.2", {"start": v(-2330.53, 787.5) * mm, "end": v(-2330.53, 754.99) * mm});
            skLineSegment(sketch, "E60.1.9.3", {"start": v(-2360.88, 787.5) * mm, "end": v(-2360.88, 754.99) * mm});
            skLineSegment(sketch, "E60.1.10.0", {"start": v(-2360.88, 859.9) * mm, "end": v(-2330.53, 859.9) * mm});
            skLineSegment(sketch, "E60.1.10.1", {"start": v(-2360.88, 827.38) * mm, "end": v(-2330.53, 827.38) * mm});
            skLineSegment(sketch, "E60.1.10.2", {"start": v(-2330.53, 859.9) * mm, "end": v(-2330.53, 827.38) * mm});
            skLineSegment(sketch, "E60.1.10.3", {"start": v(-2360.88, 859.9) * mm, "end": v(-2360.88, 827.38) * mm});
            skLineSegment(sketch, "E60.1.11.0", {"start": v(-2360.88, 932.28) * mm, "end": v(-2330.53, 932.28) * mm});
            skLineSegment(sketch, "E60.1.11.1", {"start": v(-2360.88, 899.77) * mm, "end": v(-2330.53, 899.77) * mm});
            skLineSegment(sketch, "E60.1.11.2", {"start": v(-2330.53, 932.28) * mm, "end": v(-2330.53, 899.77) * mm});
            skLineSegment(sketch, "E60.1.11.3", {"start": v(-2360.88, 932.28) * mm, "end": v(-2360.88, 899.77) * mm});
            skLineSegment(sketch, "E60.1.12.0", {"start": v(-2360.88, 1004.67) * mm, "end": v(-2330.53, 1004.67) * mm});
            skLineSegment(sketch, "E60.1.12.1", {"start": v(-2360.88, 972.16) * mm, "end": v(-2330.53, 972.16) * mm});
            skLineSegment(sketch, "E60.1.12.2", {"start": v(-2330.53, 1004.67) * mm, "end": v(-2330.53, 972.16) * mm});
            skLineSegment(sketch, "E60.1.12.3", {"start": v(-2360.88, 1004.67) * mm, "end": v(-2360.88, 972.16) * mm});
            skLineSegment(sketch, "E60.2.0.0", {"start": v(-2288.5, 136) * mm, "end": v(-2258.14, 136) * mm});
            skLineSegment(sketch, "E60.2.0.1", {"start": v(-2288.5, 103.48) * mm, "end": v(-2258.14, 103.48) * mm});
            skLineSegment(sketch, "E60.2.0.2", {"start": v(-2258.14, 136) * mm, "end": v(-2258.14, 103.48) * mm});
            skLineSegment(sketch, "E60.2.0.3", {"start": v(-2288.5, 136) * mm, "end": v(-2288.5, 103.48) * mm});
            skLineSegment(sketch, "E60.2.1.0", {"start": v(-2288.5, 208.38) * mm, "end": v(-2258.14, 208.38) * mm});
            skLineSegment(sketch, "E60.2.1.1", {"start": v(-2288.5, 175.87) * mm, "end": v(-2258.14, 175.87) * mm});
            skLineSegment(sketch, "E60.2.1.2", {"start": v(-2258.14, 208.38) * mm, "end": v(-2258.14, 175.87) * mm});
            skLineSegment(sketch, "E60.2.1.3", {"start": v(-2288.5, 208.38) * mm, "end": v(-2288.5, 175.87) * mm});
            skLineSegment(sketch, "E60.2.3.0", {"start": v(-2288.5, 353.16) * mm, "end": v(-2258.14, 353.16) * mm});
            skLineSegment(sketch, "E60.2.3.1", {"start": v(-2288.5, 320.65) * mm, "end": v(-2258.14, 320.65) * mm});
            skLineSegment(sketch, "E60.2.3.2", {"start": v(-2258.14, 353.16) * mm, "end": v(-2258.14, 320.65) * mm});
            skLineSegment(sketch, "E60.2.3.3", {"start": v(-2288.5, 353.16) * mm, "end": v(-2288.5, 320.65) * mm});
            skLineSegment(sketch, "E60.2.4.0", {"start": v(-2288.5, 425.55) * mm, "end": v(-2258.14, 425.55) * mm});
            skLineSegment(sketch, "E60.2.4.1", {"start": v(-2288.5, 393.04) * mm, "end": v(-2258.14, 393.04) * mm});
            skLineSegment(sketch, "E60.2.4.2", {"start": v(-2258.14, 425.55) * mm, "end": v(-2258.14, 393.04) * mm});
            skLineSegment(sketch, "E60.2.4.3", {"start": v(-2288.5, 425.55) * mm, "end": v(-2288.5, 393.04) * mm});
            skLineSegment(sketch, "E60.2.5.0", {"start": v(-2288.5, 497.94) * mm, "end": v(-2258.14, 497.94) * mm});
            skLineSegment(sketch, "E60.2.5.1", {"start": v(-2288.5, 465.43) * mm, "end": v(-2258.14, 465.43) * mm});
            skLineSegment(sketch, "E60.2.5.2", {"start": v(-2258.14, 497.94) * mm, "end": v(-2258.14, 465.43) * mm});
            skLineSegment(sketch, "E60.2.5.3", {"start": v(-2288.5, 497.94) * mm, "end": v(-2288.5, 465.43) * mm});
            skLineSegment(sketch, "E60.2.6.0", {"start": v(-2288.5, 570.33) * mm, "end": v(-2258.14, 570.33) * mm});
            skLineSegment(sketch, "E60.2.6.1", {"start": v(-2288.5, 537.82) * mm, "end": v(-2258.14, 537.82) * mm});
            skLineSegment(sketch, "E60.2.6.2", {"start": v(-2258.14, 570.33) * mm, "end": v(-2258.14, 537.82) * mm});
            skLineSegment(sketch, "E60.2.6.3", {"start": v(-2288.5, 570.33) * mm, "end": v(-2288.5, 537.82) * mm});
            skLineSegment(sketch, "E60.2.7.0", {"start": v(-2288.5, 642.72) * mm, "end": v(-2258.14, 642.72) * mm});
            skLineSegment(sketch, "E60.2.7.1", {"start": v(-2288.5, 610.2) * mm, "end": v(-2258.14, 610.2) * mm});
            skLineSegment(sketch, "E60.2.7.2", {"start": v(-2258.14, 642.72) * mm, "end": v(-2258.14, 610.2) * mm});
            skLineSegment(sketch, "E60.2.7.3", {"start": v(-2288.5, 642.72) * mm, "end": v(-2288.5, 610.2) * mm});
            skLineSegment(sketch, "E60.2.8.0", {"start": v(-2288.5, 715.11) * mm, "end": v(-2258.14, 715.11) * mm});
            skLineSegment(sketch, "E60.2.8.1", {"start": v(-2288.5, 682.6) * mm, "end": v(-2258.14, 682.6) * mm});
            skLineSegment(sketch, "E60.2.8.2", {"start": v(-2258.14, 715.11) * mm, "end": v(-2258.14, 682.6) * mm});
            skLineSegment(sketch, "E60.2.8.3", {"start": v(-2288.5, 715.11) * mm, "end": v(-2288.5, 682.6) * mm});
            skLineSegment(sketch, "E60.2.9.0", {"start": v(-2288.5, 787.5) * mm, "end": v(-2258.14, 787.5) * mm});
            skLineSegment(sketch, "E60.2.9.1", {"start": v(-2288.5, 754.99) * mm, "end": v(-2258.14, 754.99) * mm});
            skLineSegment(sketch, "E60.2.9.2", {"start": v(-2258.14, 787.5) * mm, "end": v(-2258.14, 754.99) * mm});
            skLineSegment(sketch, "E60.2.9.3", {"start": v(-2288.5, 787.5) * mm, "end": v(-2288.5, 754.99) * mm});
            skLineSegment(sketch, "E60.2.11.0", {"start": v(-2288.5, 932.28) * mm, "end": v(-2258.14, 932.28) * mm});
            skLineSegment(sketch, "E60.2.11.1", {"start": v(-2288.5, 899.77) * mm, "end": v(-2258.14, 899.77) * mm});
            skLineSegment(sketch, "E60.2.11.2", {"start": v(-2258.14, 932.28) * mm, "end": v(-2258.14, 899.77) * mm});
            skLineSegment(sketch, "E60.2.11.3", {"start": v(-2288.5, 932.28) * mm, "end": v(-2288.5, 899.77) * mm});
            skLineSegment(sketch, "E60.2.12.0", {"start": v(-2288.5, 1004.67) * mm, "end": v(-2258.14, 1004.67) * mm});
            skLineSegment(sketch, "E60.2.12.1", {"start": v(-2288.5, 972.16) * mm, "end": v(-2258.14, 972.16) * mm});
            skLineSegment(sketch, "E60.2.12.2", {"start": v(-2258.14, 1004.67) * mm, "end": v(-2258.14, 972.16) * mm});
            skLineSegment(sketch, "E60.2.12.3", {"start": v(-2288.5, 1004.67) * mm, "end": v(-2288.5, 972.16) * mm});
            skLineSegment(sketch, "E60.direction1", {"start": v(-2433.27, 136) * mm, "end": v(-2360.88, 136) * mm, "construction": true});
            skLineSegment(sketch, "E60.direction2", {"start": v(-2433.27, 136) * mm, "end": v(-2433.27, 208.38) * mm, "construction": true});
            skLineSegment(sketch, "E61.0.3.0", {"start": v(-2216.1, 136) * mm, "end": v(-2185.75, 136) * mm});
            skLineSegment(sketch, "E61.3.3.0", {"start": v(-2216.1, 103.48) * mm, "end": v(-2185.75, 103.48) * mm});
            skLineSegment(sketch, "E61.6.3.0", {"start": v(-2185.75, 136) * mm, "end": v(-2185.75, 103.48) * mm});
            skLineSegment(sketch, "E61.9.3.0", {"start": v(-2216.1, 136) * mm, "end": v(-2216.1, 103.48) * mm});
            skLineSegment(sketch, "E61.0.3.1", {"start": v(-2216.1, 208.38) * mm, "end": v(-2185.75, 208.38) * mm});
            skLineSegment(sketch, "E61.3.3.1", {"start": v(-2216.1, 175.87) * mm, "end": v(-2185.75, 175.87) * mm});
            skLineSegment(sketch, "E61.6.3.1", {"start": v(-2185.75, 208.38) * mm, "end": v(-2185.75, 175.87) * mm});
            skLineSegment(sketch, "E61.9.3.1", {"start": v(-2216.1, 208.38) * mm, "end": v(-2216.1, 175.87) * mm});
            skLineSegment(sketch, "E61.0.3.2", {"start": v(-2216.1, 280.77) * mm, "end": v(-2185.75, 280.77) * mm});
            skLineSegment(sketch, "E61.3.3.2", {"start": v(-2216.1, 248.26) * mm, "end": v(-2185.75, 248.26) * mm});
            skLineSegment(sketch, "E61.6.3.2", {"start": v(-2185.75, 280.77) * mm, "end": v(-2185.75, 248.26) * mm});
            skLineSegment(sketch, "E61.9.3.2", {"start": v(-2216.1, 280.77) * mm, "end": v(-2216.1, 248.26) * mm});
            skLineSegment(sketch, "E61.0.3.3", {"start": v(-2216.1, 353.16) * mm, "end": v(-2185.75, 353.16) * mm});
            skLineSegment(sketch, "E61.3.3.3", {"start": v(-2216.1, 320.65) * mm, "end": v(-2185.75, 320.65) * mm});
            skLineSegment(sketch, "E61.6.3.3", {"start": v(-2185.75, 353.16) * mm, "end": v(-2185.75, 320.65) * mm});
            skLineSegment(sketch, "E61.9.3.3", {"start": v(-2216.1, 353.16) * mm, "end": v(-2216.1, 320.65) * mm});
            skLineSegment(sketch, "E61.0.3.4", {"start": v(-2216.1, 425.55) * mm, "end": v(-2185.75, 425.55) * mm});
            skLineSegment(sketch, "E61.3.3.4", {"start": v(-2216.1, 393.04) * mm, "end": v(-2185.75, 393.04) * mm});
            skLineSegment(sketch, "E61.6.3.4", {"start": v(-2185.75, 425.55) * mm, "end": v(-2185.75, 393.04) * mm});
            skLineSegment(sketch, "E61.9.3.4", {"start": v(-2216.1, 425.55) * mm, "end": v(-2216.1, 393.04) * mm});
            skLineSegment(sketch, "E61.0.3.5", {"start": v(-2216.1, 497.94) * mm, "end": v(-2185.75, 497.94) * mm});
            skLineSegment(sketch, "E61.3.3.5", {"start": v(-2216.1, 465.43) * mm, "end": v(-2185.75, 465.43) * mm});
            skLineSegment(sketch, "E61.6.3.5", {"start": v(-2185.75, 497.94) * mm, "end": v(-2185.75, 465.43) * mm});
            skLineSegment(sketch, "E61.9.3.5", {"start": v(-2216.1, 497.94) * mm, "end": v(-2216.1, 465.43) * mm});
            skLineSegment(sketch, "E61.0.3.6", {"start": v(-2216.1, 570.33) * mm, "end": v(-2185.75, 570.33) * mm});
            skLineSegment(sketch, "E61.3.3.6", {"start": v(-2216.1, 537.82) * mm, "end": v(-2185.75, 537.82) * mm});
            skLineSegment(sketch, "E61.6.3.6", {"start": v(-2185.75, 570.33) * mm, "end": v(-2185.75, 537.82) * mm});
            skLineSegment(sketch, "E61.9.3.6", {"start": v(-2216.1, 570.33) * mm, "end": v(-2216.1, 537.82) * mm});
            skLineSegment(sketch, "E61.0.3.7", {"start": v(-2216.1, 642.72) * mm, "end": v(-2185.75, 642.72) * mm});
            skLineSegment(sketch, "E61.3.3.7", {"start": v(-2216.1, 610.2) * mm, "end": v(-2185.75, 610.2) * mm});
            skLineSegment(sketch, "E61.6.3.7", {"start": v(-2185.75, 642.72) * mm, "end": v(-2185.75, 610.2) * mm});
            skLineSegment(sketch, "E61.9.3.7", {"start": v(-2216.1, 642.72) * mm, "end": v(-2216.1, 610.2) * mm});
            skLineSegment(sketch, "E61.0.3.8", {"start": v(-2216.1, 715.11) * mm, "end": v(-2185.75, 715.11) * mm});
            skLineSegment(sketch, "E61.3.3.8", {"start": v(-2216.1, 682.6) * mm, "end": v(-2185.75, 682.6) * mm});
            skLineSegment(sketch, "E61.6.3.8", {"start": v(-2185.75, 715.11) * mm, "end": v(-2185.75, 682.6) * mm});
            skLineSegment(sketch, "E61.9.3.8", {"start": v(-2216.1, 715.11) * mm, "end": v(-2216.1, 682.6) * mm});
            skLineSegment(sketch, "E61.0.3.9", {"start": v(-2216.1, 787.5) * mm, "end": v(-2185.75, 787.5) * mm});
            skLineSegment(sketch, "E61.3.3.9", {"start": v(-2216.1, 754.99) * mm, "end": v(-2185.75, 754.99) * mm});
            skLineSegment(sketch, "E61.6.3.9", {"start": v(-2185.75, 787.5) * mm, "end": v(-2185.75, 754.99) * mm});
            skLineSegment(sketch, "E61.9.3.9", {"start": v(-2216.1, 787.5) * mm, "end": v(-2216.1, 754.99) * mm});
            skLineSegment(sketch, "E61.0.3.11", {"start": v(-2216.1, 932.28) * mm, "end": v(-2185.75, 932.28) * mm});
            skLineSegment(sketch, "E61.3.3.11", {"start": v(-2216.1, 899.77) * mm, "end": v(-2185.75, 899.77) * mm});
            skLineSegment(sketch, "E61.6.3.11", {"start": v(-2185.75, 932.28) * mm, "end": v(-2185.75, 899.77) * mm});
            skLineSegment(sketch, "E61.9.3.11", {"start": v(-2216.1, 932.28) * mm, "end": v(-2216.1, 899.77) * mm});
            skLineSegment(sketch, "E61.0.3.12", {"start": v(-2216.1, 1004.67) * mm, "end": v(-2185.75, 1004.67) * mm});
            skLineSegment(sketch, "E61.3.3.12", {"start": v(-2216.1, 972.16) * mm, "end": v(-2185.75, 972.16) * mm});
            skLineSegment(sketch, "E61.6.3.12", {"start": v(-2185.75, 1004.67) * mm, "end": v(-2185.75, 972.16) * mm});
            skLineSegment(sketch, "E61.9.3.12", {"start": v(-2216.1, 1004.67) * mm, "end": v(-2216.1, 972.16) * mm});
            skLineSegment(sketch, "E62.0.4.0", {"start": v(-2143.71, 136) * mm, "end": v(-2113.36, 136) * mm});
            skLineSegment(sketch, "E62.3.4.0", {"start": v(-2143.71, 103.48) * mm, "end": v(-2113.36, 103.48) * mm});
            skLineSegment(sketch, "E62.6.4.0", {"start": v(-2113.36, 136) * mm, "end": v(-2113.36, 103.48) * mm});
            skLineSegment(sketch, "E62.9.4.0", {"start": v(-2143.71, 136) * mm, "end": v(-2143.71, 103.48) * mm});
            skLineSegment(sketch, "E62.0.4.1", {"start": v(-2143.71, 208.38) * mm, "end": v(-2113.36, 208.38) * mm});
            skLineSegment(sketch, "E62.3.4.1", {"start": v(-2143.71, 175.87) * mm, "end": v(-2113.36, 175.87) * mm});
            skLineSegment(sketch, "E62.6.4.1", {"start": v(-2113.36, 208.38) * mm, "end": v(-2113.36, 175.87) * mm});
            skLineSegment(sketch, "E62.9.4.1", {"start": v(-2143.71, 208.38) * mm, "end": v(-2143.71, 175.87) * mm});
            skLineSegment(sketch, "E62.0.4.2", {"start": v(-2143.71, 280.77) * mm, "end": v(-2113.36, 280.77) * mm});
            skLineSegment(sketch, "E62.3.4.2", {"start": v(-2143.71, 248.26) * mm, "end": v(-2113.36, 248.26) * mm});
            skLineSegment(sketch, "E62.6.4.2", {"start": v(-2113.36, 280.77) * mm, "end": v(-2113.36, 248.26) * mm});
            skLineSegment(sketch, "E62.9.4.2", {"start": v(-2143.71, 280.77) * mm, "end": v(-2143.71, 248.26) * mm});
            skLineSegment(sketch, "E62.0.4.3", {"start": v(-2143.71, 353.16) * mm, "end": v(-2113.36, 353.16) * mm});
            skLineSegment(sketch, "E62.3.4.3", {"start": v(-2143.71, 320.65) * mm, "end": v(-2113.36, 320.65) * mm});
            skLineSegment(sketch, "E62.6.4.3", {"start": v(-2113.36, 353.16) * mm, "end": v(-2113.36, 320.65) * mm});
            skLineSegment(sketch, "E62.9.4.3", {"start": v(-2143.71, 353.16) * mm, "end": v(-2143.71, 320.65) * mm});
            skLineSegment(sketch, "E62.0.4.4", {"start": v(-2143.71, 425.55) * mm, "end": v(-2113.36, 425.55) * mm});
            skLineSegment(sketch, "E62.3.4.4", {"start": v(-2143.71, 393.04) * mm, "end": v(-2113.36, 393.04) * mm});
            skLineSegment(sketch, "E62.6.4.4", {"start": v(-2113.36, 425.55) * mm, "end": v(-2113.36, 393.04) * mm});
            skLineSegment(sketch, "E62.9.4.4", {"start": v(-2143.71, 425.55) * mm, "end": v(-2143.71, 393.04) * mm});
            skLineSegment(sketch, "E62.0.4.5", {"start": v(-2143.71, 497.94) * mm, "end": v(-2113.36, 497.94) * mm});
            skLineSegment(sketch, "E62.3.4.5", {"start": v(-2143.71, 465.43) * mm, "end": v(-2113.36, 465.43) * mm});
            skLineSegment(sketch, "E62.6.4.5", {"start": v(-2113.36, 497.94) * mm, "end": v(-2113.36, 465.43) * mm});
            skLineSegment(sketch, "E62.9.4.5", {"start": v(-2143.71, 497.94) * mm, "end": v(-2143.71, 465.43) * mm});
            skLineSegment(sketch, "E62.0.4.6", {"start": v(-2143.71, 570.33) * mm, "end": v(-2113.36, 570.33) * mm});
            skLineSegment(sketch, "E62.3.4.6", {"start": v(-2143.71, 537.82) * mm, "end": v(-2113.36, 537.82) * mm});
            skLineSegment(sketch, "E62.6.4.6", {"start": v(-2113.36, 570.33) * mm, "end": v(-2113.36, 537.82) * mm});
            skLineSegment(sketch, "E62.9.4.6", {"start": v(-2143.71, 570.33) * mm, "end": v(-2143.71, 537.82) * mm});
            skLineSegment(sketch, "E62.0.4.7", {"start": v(-2143.71, 642.72) * mm, "end": v(-2113.36, 642.72) * mm});
            skLineSegment(sketch, "E62.3.4.7", {"start": v(-2143.71, 610.2) * mm, "end": v(-2113.36, 610.2) * mm});
            skLineSegment(sketch, "E62.6.4.7", {"start": v(-2113.36, 642.72) * mm, "end": v(-2113.36, 610.2) * mm});
            skLineSegment(sketch, "E62.9.4.7", {"start": v(-2143.71, 642.72) * mm, "end": v(-2143.71, 610.2) * mm});
            skLineSegment(sketch, "E62.0.4.8", {"start": v(-2143.71, 715.11) * mm, "end": v(-2113.36, 715.11) * mm});
            skLineSegment(sketch, "E62.3.4.8", {"start": v(-2143.71, 682.6) * mm, "end": v(-2113.36, 682.6) * mm});
            skLineSegment(sketch, "E62.6.4.8", {"start": v(-2113.36, 715.11) * mm, "end": v(-2113.36, 682.6) * mm});
            skLineSegment(sketch, "E62.9.4.8", {"start": v(-2143.71, 715.11) * mm, "end": v(-2143.71, 682.6) * mm});
            skLineSegment(sketch, "E62.0.4.9", {"start": v(-2143.71, 787.5) * mm, "end": v(-2113.36, 787.5) * mm});
            skLineSegment(sketch, "E62.3.4.9", {"start": v(-2143.71, 754.99) * mm, "end": v(-2113.36, 754.99) * mm});
            skLineSegment(sketch, "E62.6.4.9", {"start": v(-2113.36, 787.5) * mm, "end": v(-2113.36, 754.99) * mm});
            skLineSegment(sketch, "E62.9.4.9", {"start": v(-2143.71, 787.5) * mm, "end": v(-2143.71, 754.99) * mm});
            skLineSegment(sketch, "E62.0.4.11", {"start": v(-2143.71, 932.28) * mm, "end": v(-2113.36, 932.28) * mm});
            skLineSegment(sketch, "E62.3.4.11", {"start": v(-2143.71, 899.77) * mm, "end": v(-2113.36, 899.77) * mm});
            skLineSegment(sketch, "E62.6.4.11", {"start": v(-2113.36, 932.28) * mm, "end": v(-2113.36, 899.77) * mm});
            skLineSegment(sketch, "E62.9.4.11", {"start": v(-2143.71, 932.28) * mm, "end": v(-2143.71, 899.77) * mm});
            skLineSegment(sketch, "E62.0.4.12", {"start": v(-2143.71, 1004.67) * mm, "end": v(-2113.36, 1004.67) * mm});
            skLineSegment(sketch, "E62.3.4.12", {"start": v(-2143.71, 972.16) * mm, "end": v(-2113.36, 972.16) * mm});
            skLineSegment(sketch, "E62.6.4.12", {"start": v(-2113.36, 1004.67) * mm, "end": v(-2113.36, 972.16) * mm});
            skLineSegment(sketch, "E62.9.4.12", {"start": v(-2143.71, 1004.67) * mm, "end": v(-2143.71, 972.16) * mm});
            skLineSegment(sketch, "E63.bottom", {"start": v(2634.13, -409.62) * mm, "end": v(2953.31, -409.62) * mm});
            skLineSegment(sketch, "E63.top", {"start": v(2634.13, -525.7) * mm, "end": v(2953.31, -525.7) * mm});
            skLineSegment(sketch, "E63.left", {"start": v(2634.13, -409.62) * mm, "end": v(2634.13, -525.7) * mm});
            skLineSegment(sketch, "E63.right", {"start": v(2953.31, -409.62) * mm, "end": v(2953.31, -525.7) * mm});
            skLineSegment(sketch, "E64.top", {"start": v(2225.8, -306.45) * mm, "end": v(2287.06, -306.45) * mm});
            skLineSegment(sketch, "E64.left", {"start": v(2225.8, -238.75) * mm, "end": v(2225.8, -306.45) * mm});
            skLineSegment(sketch, "E64.right", {"start": v(2287.06, -238.75) * mm, "end": v(2287.06, -306.45) * mm});
            skLineSegment(sketch, "E65", {"start": v(2256.44, -182.42) * mm, "end": v(2237.57, -182.42) * mm});
            skPoint(sketch, "E65.startSnap0", {"position": v(2256.44, -238.75) * mm});
            skLineSegment(sketch, "E66", {"start": v(2237.57, -182.42) * mm, "end": v(2225.8, -238.75) * mm});
            skLineSegment(sketch, "E67", {"start": v(2256.44, -182.42) * mm, "end": v(2256.44, -238.75) * mm, "construction": true});
            skLineSegment(sketch, "E68.MirrorCS", {"start": v(2275.3, -182.42) * mm, "end": v(2287.06, -238.75) * mm});
            skLineSegment(sketch, "E69.MirrorCS", {"start": v(2256.44, -182.42) * mm, "end": v(2275.3, -182.42) * mm});
            skPoint(sketch, "E70.MirrorCS.end.orphan", {"position": v(2237.57, -182.42) * mm});
            skPoint(sketch, "E70.MirrorCS.start.orphan", {"position": v(2220.27, -174.87) * mm});
            skPoint(sketch, "E71.orphan", {"position": v(2532.34, -329.92) * mm});
            skLineSegment(sketch, "E72", {"start": v(-2529.86, 1037.73) * mm, "end": v(-2529.86, 311.62) * mm});
            skLineSegment(sketch, "E73", {"start": v(-3342.52, -205.86) * mm, "end": v(-3342.52, 739.04) * mm});
            skLineSegment(sketch, "E74.trimOffspring", {"start": v(-2529.86, 1037.73) * mm, "end": v(-2016.7, 1037.73) * mm});
            skLineSegment(sketch, "E75.top", {"start": v(-3079.58, 1305.87) * mm, "end": v(-2875.76, 1305.87) * mm});
            skLineSegment(sketch, "E75.left", {"start": v(-3079.58, -205.86) * mm, "end": v(-3079.58, 1305.87) * mm});
            skLineSegment(sketch, "E76.trimOffspring", {"start": v(-3079.58, -205.86) * mm, "end": v(-3342.52, -205.86) * mm});
            skLineSegment(sketch, "E77", {"start": v(4106.83, -55.58) * mm, "end": v(4426.26, -206.26) * mm});
            skLineSegment(sketch, "E78", {"start": v(4426.26, -206.26) * mm, "end": v(4426.26, 339.93) * mm});
            skLineSegment(sketch, "E79", {"start": v(4426.26, 339.93) * mm, "end": v(5078.19, 339.93) * mm});
            skLineSegment(sketch, "E80", {"start": v(5078.19, 339.93) * mm, "end": v(5078.19, -547.29) * mm});
            skLineSegment(sketch, "E81", {"start": v(3205.33, -108.87) * mm, "end": v(3336.86, -337.22) * mm});
            skLineSegment(sketch, "E82", {"start": v(3336.86, -337.22) * mm, "end": v(3354.78, -337.22) * mm});
            skLineSegment(sketch, "E83", {"start": v(3354.78, -337.22) * mm, "end": v(3536.68, 0) * mm});
            skLineSegment(sketch, "E84", {"start": v(3624.87, 0) * mm, "end": v(3826.66, -337.27) * mm});
            skLineSegment(sketch, "E85", {"start": v(3826.66, -337.27) * mm, "end": v(4011.7, -60.25) * mm});
            skLineSegment(sketch, "E86", {"start": v(4011.7, -60.25) * mm, "end": v(4106.83, -55.58) * mm});
            skPoint(sketch, "E87.orphan", {"position": v(3989.02, 0) * mm});
            skLineSegment(sketch, "E88", {"start": v(-2762.84, 311.62) * mm, "end": v(-2529.86, 311.62) * mm});
            skLineSegment(sketch, "E89", {"start": v(-2875.76, 1305.87) * mm, "end": v(-2762.84, 799.4) * mm});
            skLineSegment(sketch, "E90", {"start": v(-2762.84, 799.4) * mm, "end": v(-2762.84, 311.62) * mm});
            skLineSegment(sketch, "E91", {"start": v(-3487.34, 739.04) * mm, "end": v(-3487.34, 182.25) * mm});
            skLineSegment(sketch, "E92", {"start": v(2273.89, -90.17) * mm, "end": v(2549.54, -345.87) * mm});
            skLineSegment(sketch, "E93", {"start": v(2244.2, -90.17) * mm, "end": v(2273.89, -90.17) * mm});
            skLineSegment(sketch, "E94", {"start": v(2725.07, -144.63) * mm, "end": v(2768.68, -144.63) * mm});
            skLineSegment(sketch, "E95", {"start": v(3130.64, -108.87) * mm, "end": v(3205.33, -108.87) * mm});
            skLineSegment(sketch, "E96", {"start": v(3130.64, -108.87) * mm, "end": v(2987.94, -346.12) * mm});
            skPoint(sketch, "E97.orphan", {"position": v(3500.79, 0) * mm});
            skLineSegment(sketch, "E98", {"start": v(3536.68, 0) * mm, "end": v(3624.87, 0) * mm});
            skLineSegment(sketch, "E99", {"start": v(-4050, -267.9) * mm, "end": v(-4050, -823.15) * mm});
            skLineSegment(sketch, "E100", {"start": v(-200, 2209.1) * mm, "end": v(-200, -598.62) * mm});
            skLineSegment(sketch, "E101", {"start": v(200, 2209.1) * mm, "end": v(200, 981.37) * mm});
            skPoint(sketch, "E102.end.orphan", {"position": v(4426.26, 66.83) * mm});
            skPoint(sketch, "E102.start.orphan", {"position": v(2001.46, 0) * mm});
            skLineSegment(sketch, "E103", {"start": v(200, -823.15) * mm, "end": v(5530, -823.15) * mm});
            skLineSegment(sketch, "E104", {"start": v(819.93, 718.46) * mm, "end": v(819.93, -498.19) * mm});
            skLineSegment(sketch, "E105", {"start": v(819.93, -498.19) * mm, "end": v(840.6, -498.19) * mm});
            skLineSegment(sketch, "E106", {"start": v(840.6, -498.19) * mm, "end": v(840.6, 718.46) * mm});
            skLineSegment(sketch, "E107", {"start": v(-3487.34, 739.04) * mm, "end": v(-3342.52, 739.04) * mm});
            skLineSegment(sketch, "E108", {"start": v(246.5, 883.06) * mm, "end": v(246.5, 788.62) * mm});
            skLineSegment(sketch, "E109.trimOffspring", {"start": v(246.5, 883.06) * mm, "end": v(677.5, 883.06) * mm});
            skLineSegment(sketch, "E110.trimOffspring", {"start": v(246.5, 121.06) * mm, "end": v(246.5, 26.62) * mm});
            skLineSegment(sketch, "E111.trimOffspring", {"start": v(246.5, 375.06) * mm, "end": v(246.5, 280.62) * mm});
            skPoint(sketch, "E112.orphan", {"position": v(246.5, -823.15) * mm});
            skLineSegment(sketch, "E113.trimOffspring", {"start": v(246.5, -132.94) * mm, "end": v(246.5, -227.38) * mm});
            skLineSegment(sketch, "E114", {"start": v(677.5, 788.62) * mm, "end": v(246.5, 788.62) * mm});
            skLineSegment(sketch, "E115", {"start": v(246.5, 629.06) * mm, "end": v(246.5, 534.62) * mm});
            skLineSegment(sketch, "E116.bottom", {"start": v(1822.23, 591.6) * mm, "end": v(1867.4, 591.6) * mm});
            skLineSegment(sketch, "E116.top", {"start": v(1822.23, 543.32) * mm, "end": v(1867.4, 543.32) * mm});
            skLineSegment(sketch, "E116.left", {"start": v(1822.23, 591.6) * mm, "end": v(1822.23, 543.32) * mm});
            skLineSegment(sketch, "E116.right", {"start": v(1867.4, 591.6) * mm, "end": v(1867.4, 543.32) * mm});
            skLineSegment(sketch, "E117.bottom", {"start": v(1918.99, 591.6) * mm, "end": v(1964.15, 591.6) * mm});
            skLineSegment(sketch, "E117.top", {"start": v(1918.99, 543.32) * mm, "end": v(1964.15, 543.32) * mm});
            skLineSegment(sketch, "E117.left", {"start": v(1918.99, 591.6) * mm, "end": v(1918.99, 543.32) * mm});
            skLineSegment(sketch, "E117.right", {"start": v(1964.15, 591.6) * mm, "end": v(1964.15, 543.32) * mm});
            skLineSegment(sketch, "E118.0.1.0", {"start": v(1867.4, 460.6) * mm, "end": v(1867.4, 412.32) * mm});
            skLineSegment(sketch, "E118.0.1.1", {"start": v(1918.99, 460.6) * mm, "end": v(1964.15, 460.6) * mm});
            skLineSegment(sketch, "E118.0.1.2", {"start": v(1964.15, 460.6) * mm, "end": v(1964.15, 412.32) * mm});
            skLineSegment(sketch, "E118.0.1.3", {"start": v(1918.99, 460.6) * mm, "end": v(1918.99, 412.32) * mm});
            skLineSegment(sketch, "E118.0.1.4", {"start": v(1918.99, 412.32) * mm, "end": v(1964.15, 412.32) * mm});
            skLineSegment(sketch, "E118.0.1.5", {"start": v(1822.23, 460.6) * mm, "end": v(1867.4, 460.6) * mm});
            skLineSegment(sketch, "E118.0.1.6", {"start": v(1822.23, 460.6) * mm, "end": v(1822.23, 412.32) * mm});
            skLineSegment(sketch, "E118.0.1.7", {"start": v(1822.23, 412.32) * mm, "end": v(1867.4, 412.32) * mm});
            skLineSegment(sketch, "E118.0.2.1", {"start": v(1918.99, 329.6) * mm, "end": v(1964.15, 329.6) * mm});
            skLineSegment(sketch, "E118.0.2.2", {"start": v(1964.15, 329.6) * mm, "end": v(1964.15, 281.32) * mm});
            skLineSegment(sketch, "E118.0.2.3", {"start": v(1918.99, 329.6) * mm, "end": v(1918.99, 281.32) * mm});
            skLineSegment(sketch, "E118.0.2.4", {"start": v(1918.99, 281.32) * mm, "end": v(1964.15, 281.32) * mm});
            skLineSegment(sketch, "E118.0.3.0", {"start": v(1867.4, 198.6) * mm, "end": v(1867.4, 150.32) * mm});
            skLineSegment(sketch, "E118.0.3.1", {"start": v(1918.99, 198.6) * mm, "end": v(1964.15, 198.6) * mm});
            skLineSegment(sketch, "E118.0.3.2", {"start": v(1964.15, 198.6) * mm, "end": v(1964.15, 150.32) * mm});
            skLineSegment(sketch, "E118.0.3.3", {"start": v(1918.99, 198.6) * mm, "end": v(1918.99, 150.32) * mm});
            skLineSegment(sketch, "E118.0.3.4", {"start": v(1918.99, 150.32) * mm, "end": v(1964.15, 150.32) * mm});
            skLineSegment(sketch, "E118.0.3.5", {"start": v(1822.23, 198.6) * mm, "end": v(1867.4, 198.6) * mm});
            skLineSegment(sketch, "E118.0.3.6", {"start": v(1822.23, 198.6) * mm, "end": v(1822.23, 150.32) * mm});
            skLineSegment(sketch, "E118.0.3.7", {"start": v(1822.23, 150.32) * mm, "end": v(1867.4, 150.32) * mm});
            skLineSegment(sketch, "E118.0.4.1", {"start": v(1918.99, 67.6) * mm, "end": v(1964.15, 67.6) * mm});
            skLineSegment(sketch, "E118.0.4.2", {"start": v(1964.15, 67.6) * mm, "end": v(1964.15, 19.32) * mm});
            skLineSegment(sketch, "E118.0.4.3", {"start": v(1918.99, 67.6) * mm, "end": v(1918.99, 19.32) * mm});
            skLineSegment(sketch, "E118.0.4.4", {"start": v(1918.99, 19.32) * mm, "end": v(1964.15, 19.32) * mm});
            skLineSegment(sketch, "E118.0.5.0", {"start": v(1867.4, -63.4) * mm, "end": v(1867.4, -111.68) * mm});
            skLineSegment(sketch, "E118.0.5.1", {"start": v(1918.99, -63.4) * mm, "end": v(1964.15, -63.4) * mm});
            skLineSegment(sketch, "E118.0.5.2", {"start": v(1964.15, -63.4) * mm, "end": v(1964.15, -111.68) * mm});
            skLineSegment(sketch, "E118.0.5.3", {"start": v(1918.99, -63.4) * mm, "end": v(1918.99, -111.68) * mm});
            skLineSegment(sketch, "E118.0.5.4", {"start": v(1918.99, -111.68) * mm, "end": v(1964.15, -111.68) * mm});
            skLineSegment(sketch, "E118.0.5.5", {"start": v(1822.23, -63.4) * mm, "end": v(1867.4, -63.4) * mm});
            skLineSegment(sketch, "E118.0.5.6", {"start": v(1822.23, -63.4) * mm, "end": v(1822.23, -111.68) * mm});
            skLineSegment(sketch, "E118.0.5.7", {"start": v(1822.23, -111.68) * mm, "end": v(1867.4, -111.68) * mm});
            skLineSegment(sketch, "E118.0.6.0", {"start": v(1867.4, -194.4) * mm, "end": v(1867.4, -242.68) * mm});
            skLineSegment(sketch, "E118.0.6.5", {"start": v(1822.23, -194.4) * mm, "end": v(1867.4, -194.4) * mm});
            skLineSegment(sketch, "E118.0.6.6", {"start": v(1822.23, -194.4) * mm, "end": v(1822.23, -242.68) * mm});
            skLineSegment(sketch, "E118.0.6.7", {"start": v(1822.23, -242.68) * mm, "end": v(1867.4, -242.68) * mm});
            skLineSegment(sketch, "E118.direction1", {"start": v(1867.4, 543.32) * mm, "end": v(1892.4, 543.32) * mm, "construction": true});
            skLineSegment(sketch, "E118.direction2", {"start": v(1867.4, 543.32) * mm, "end": v(1867.4, 412.32) * mm, "construction": true});
            skLineSegment(sketch, "E119.bottom", {"start": v(4036.2, -625.01) * mm, "end": v(4124.3, -625.01) * mm});
            skLineSegment(sketch, "E119.top", {"start": v(4036.2, -823.15) * mm, "end": v(4124.3, -823.15) * mm});
            skLineSegment(sketch, "E119.left", {"start": v(4036.2, -625.01) * mm, "end": v(4036.2, -823.15) * mm});
            skLineSegment(sketch, "E119.right", {"start": v(4124.3, -625.01) * mm, "end": v(4124.3, -823.15) * mm});
            skLineSegment(sketch, "E120.bottom", {"start": v(4499.18, 258.75) * mm, "end": v(4648.3, 258.75) * mm});
            skLineSegment(sketch, "E120.left", {"start": v(4499.18, 258.75) * mm, "end": v(4499.18, 125.31) * mm});
            skLineSegment(sketch, "E120.right", {"start": v(4648.3, 258.75) * mm, "end": v(4648.3, 125.31) * mm});
            skLineSegment(sketch, "E121.0.1.0", {"start": v(4499.18, 68.75) * mm, "end": v(4499.18, -64.69) * mm});
            skLineSegment(sketch, "E121.0.1.1", {"start": v(4499.18, 68.75) * mm, "end": v(4648.3, 68.75) * mm});
            skLineSegment(sketch, "E121.0.1.2", {"start": v(4648.3, 68.75) * mm, "end": v(4648.3, -64.69) * mm});
            skLineSegment(sketch, "E121.0.2.0", {"start": v(4499.18, -121.25) * mm, "end": v(4499.18, -254.69) * mm});
            skLineSegment(sketch, "E121.0.2.1", {"start": v(4499.18, -121.25) * mm, "end": v(4648.3, -121.25) * mm});
            skLineSegment(sketch, "E121.0.2.2", {"start": v(4648.3, -121.25) * mm, "end": v(4648.3, -254.69) * mm});
            skLineSegment(sketch, "E121.0.3.0", {"start": v(4499.18, -311.25) * mm, "end": v(4499.18, -444.69) * mm});
            skLineSegment(sketch, "E121.0.3.1", {"start": v(4499.18, -311.25) * mm, "end": v(4648.3, -311.25) * mm});
            skLineSegment(sketch, "E121.0.3.2", {"start": v(4648.3, -311.25) * mm, "end": v(4648.3, -444.69) * mm});
            skLineSegment(sketch, "E121.0.4.0", {"start": v(4499.18, -501.25) * mm, "end": v(4499.18, -634.69) * mm});
            skLineSegment(sketch, "E121.0.4.1", {"start": v(4499.18, -501.25) * mm, "end": v(4648.3, -501.25) * mm});
            skLineSegment(sketch, "E121.0.4.2", {"start": v(4648.3, -501.25) * mm, "end": v(4648.3, -634.69) * mm});
            skLineSegment(sketch, "E121.1.0.0", {"start": v(4799.18, 258.75) * mm, "end": v(4799.18, 125.31) * mm});
            skLineSegment(sketch, "E121.1.0.1", {"start": v(4799.18, 258.75) * mm, "end": v(4948.3, 258.75) * mm});
            skLineSegment(sketch, "E121.1.0.2", {"start": v(4948.3, 258.75) * mm, "end": v(4948.3, 125.31) * mm});
            skLineSegment(sketch, "E121.1.1.0", {"start": v(4799.18, 68.75) * mm, "end": v(4799.18, -64.69) * mm});
            skLineSegment(sketch, "E121.1.1.1", {"start": v(4799.18, 68.75) * mm, "end": v(4948.3, 68.75) * mm});
            skLineSegment(sketch, "E121.1.1.2", {"start": v(4948.3, 68.75) * mm, "end": v(4948.3, -64.69) * mm});
            skLineSegment(sketch, "E121.1.2.0", {"start": v(4799.18, -121.25) * mm, "end": v(4799.18, -254.69) * mm});
            skLineSegment(sketch, "E121.1.2.1", {"start": v(4799.18, -121.25) * mm, "end": v(4948.3, -121.25) * mm});
            skLineSegment(sketch, "E121.1.2.2", {"start": v(4948.3, -121.25) * mm, "end": v(4948.3, -254.69) * mm});
            skLineSegment(sketch, "E121.1.3.0", {"start": v(4799.18, -311.25) * mm, "end": v(4799.18, -444.69) * mm});
            skLineSegment(sketch, "E121.1.3.1", {"start": v(4799.18, -311.25) * mm, "end": v(4948.3, -311.25) * mm});
            skLineSegment(sketch, "E121.1.3.2", {"start": v(4948.3, -311.25) * mm, "end": v(4948.3, -444.69) * mm});
            skLineSegment(sketch, "E121.1.4.0", {"start": v(4799.18, -501.25) * mm, "end": v(4799.18, -634.69) * mm});
            skLineSegment(sketch, "E121.1.4.1", {"start": v(4799.18, -501.25) * mm, "end": v(4948.3, -501.25) * mm});
            skLineSegment(sketch, "E121.1.4.2", {"start": v(4948.3, -501.25) * mm, "end": v(4948.3, -634.69) * mm});
            skLineSegment(sketch, "E121.direction2", {"start": v(4499.18, 125.31) * mm, "end": v(4499.18, -64.69) * mm, "construction": true});
            skLineSegment(sketch, "E122", {"start": v(4499.18, -634.69) * mm, "end": v(4648.3, -634.69) * mm});
            skLineSegment(sketch, "E123", {"start": v(4799.18, -634.69) * mm, "end": v(4948.3, -634.69) * mm});
            skLineSegment(sketch, "E124", {"start": v(4799.18, -444.69) * mm, "end": v(4948.3, -444.69) * mm});
            skLineSegment(sketch, "E125", {"start": v(4499.18, -444.69) * mm, "end": v(4648.3, -444.69) * mm});
            skLineSegment(sketch, "E126", {"start": v(4499.18, -254.69) * mm, "end": v(4648.3, -254.69) * mm});
            skLineSegment(sketch, "E127", {"start": v(4799.18, -254.69) * mm, "end": v(4948.3, -254.69) * mm});
            skLineSegment(sketch, "E128", {"start": v(4499.18, -64.69) * mm, "end": v(4648.3, -64.69) * mm});
            skLineSegment(sketch, "E129", {"start": v(4799.18, -64.69) * mm, "end": v(4948.3, -64.69) * mm});
            skLineSegment(sketch, "E130", {"start": v(4799.18, 125.31) * mm, "end": v(4948.3, 125.31) * mm});
            skLineSegment(sketch, "E131", {"start": v(4499.18, 125.31) * mm, "end": v(4648.3, 125.31) * mm});
            skLineSegment(sketch, "E132.0.1.0", {"start": v(-2143.71, 45) * mm, "end": v(-2143.71, 12.48) * mm});
            skLineSegment(sketch, "E132.0.1.1", {"start": v(-2288.5, 12.48) * mm, "end": v(-2258.14, 12.48) * mm});
            skLineSegment(sketch, "E132.0.1.2", {"start": v(-2288.5, 45) * mm, "end": v(-2258.14, 45) * mm});
            skLineSegment(sketch, "E132.0.1.4", {"start": v(-2258.14, 45) * mm, "end": v(-2258.14, 12.48) * mm});
            skLineSegment(sketch, "E132.0.1.6", {"start": v(-2433.27, 45) * mm, "end": v(-2433.27, 12.48) * mm});
            skLineSegment(sketch, "E132.0.1.7", {"start": v(-2360.88, 45) * mm, "end": v(-2360.88, 12.48) * mm});
            skLineSegment(sketch, "E132.0.1.8", {"start": v(-2113.36, 45) * mm, "end": v(-2113.36, 12.48) * mm});
            skLineSegment(sketch, "E132.0.1.10", {"start": v(-2288.5, 45) * mm, "end": v(-2288.5, 12.48) * mm});
            skLineSegment(sketch, "E132.0.1.11", {"start": v(-2143.71, 12.48) * mm, "end": v(-2113.36, 12.48) * mm});
            skLineSegment(sketch, "E132.0.1.12", {"start": v(-2433.27, 12.48) * mm, "end": v(-2402.92, 12.48) * mm});
            skLineSegment(sketch, "E132.0.1.13", {"start": v(-2402.92, 45) * mm, "end": v(-2402.92, 12.48) * mm});
            skLineSegment(sketch, "E132.0.1.14", {"start": v(-2433.27, 45) * mm, "end": v(-2360.88, 45) * mm, "construction": true});
            skLineSegment(sketch, "E132.0.1.15", {"start": v(-2360.88, 45) * mm, "end": v(-2330.53, 45) * mm});
            skLineSegment(sketch, "E132.0.1.16", {"start": v(-2360.88, 12.48) * mm, "end": v(-2330.53, 12.48) * mm});
            skLineSegment(sketch, "E132.0.1.18", {"start": v(-2143.71, 45) * mm, "end": v(-2113.36, 45) * mm});
            skLineSegment(sketch, "E132.0.1.19", {"start": v(-2330.53, 45) * mm, "end": v(-2330.53, 12.48) * mm});
            skLineSegment(sketch, "E132.0.1.20", {"start": v(-2433.27, 45) * mm, "end": v(-2402.92, 45) * mm});
            skLineSegment(sketch, "E132.0.2.0", {"start": v(-2143.71, -46) * mm, "end": v(-2143.71, -78.52) * mm});
            skLineSegment(sketch, "E132.0.2.1", {"start": v(-2288.5, -78.52) * mm, "end": v(-2258.14, -78.52) * mm});
            skLineSegment(sketch, "E132.0.2.2", {"start": v(-2288.5, -46) * mm, "end": v(-2258.14, -46) * mm});
            skLineSegment(sketch, "E132.0.2.4", {"start": v(-2258.14, -46) * mm, "end": v(-2258.14, -78.52) * mm});
            skLineSegment(sketch, "E132.0.2.6", {"start": v(-2433.27, -46) * mm, "end": v(-2433.27, -78.52) * mm});
            skLineSegment(sketch, "E132.0.2.7", {"start": v(-2360.88, -46) * mm, "end": v(-2360.88, -78.52) * mm});
            skLineSegment(sketch, "E132.0.2.8", {"start": v(-2113.36, -46) * mm, "end": v(-2113.36, -78.52) * mm});
            skLineSegment(sketch, "E132.0.2.10", {"start": v(-2288.5, -46) * mm, "end": v(-2288.5, -78.52) * mm});
            skLineSegment(sketch, "E132.0.2.11", {"start": v(-2143.71, -78.52) * mm, "end": v(-2113.36, -78.52) * mm});
            skLineSegment(sketch, "E132.0.2.12", {"start": v(-2433.27, -78.52) * mm, "end": v(-2402.92, -78.52) * mm});
            skLineSegment(sketch, "E132.0.2.13", {"start": v(-2402.92, -46) * mm, "end": v(-2402.92, -78.52) * mm});
            skLineSegment(sketch, "E132.0.2.14", {"start": v(-2433.27, -46) * mm, "end": v(-2360.88, -46) * mm, "construction": true});
            skLineSegment(sketch, "E132.0.2.15", {"start": v(-2360.88, -46) * mm, "end": v(-2330.53, -46) * mm});
            skLineSegment(sketch, "E132.0.2.16", {"start": v(-2360.88, -78.52) * mm, "end": v(-2330.53, -78.52) * mm});
            skLineSegment(sketch, "E132.0.2.18", {"start": v(-2143.71, -46) * mm, "end": v(-2113.36, -46) * mm});
            skLineSegment(sketch, "E132.0.2.19", {"start": v(-2330.53, -46) * mm, "end": v(-2330.53, -78.52) * mm});
            skLineSegment(sketch, "E132.0.2.20", {"start": v(-2433.27, -46) * mm, "end": v(-2402.92, -46) * mm});
            skLineSegment(sketch, "E132.0.3.0", {"start": v(-2143.71, -137) * mm, "end": v(-2143.71, -169.52) * mm});
            skLineSegment(sketch, "E132.0.3.1", {"start": v(-2288.5, -169.52) * mm, "end": v(-2258.14, -169.52) * mm});
            skLineSegment(sketch, "E132.0.3.2", {"start": v(-2288.5, -137) * mm, "end": v(-2258.14, -137) * mm});
            skLineSegment(sketch, "E132.0.3.3", {"start": v(-2185.75, -137) * mm, "end": v(-2185.75, -169.52) * mm});
            skLineSegment(sketch, "E132.0.3.4", {"start": v(-2258.14, -137) * mm, "end": v(-2258.14, -169.52) * mm});
            skLineSegment(sketch, "E132.0.3.5", {"start": v(-2216.1, -137) * mm, "end": v(-2216.1, -169.52) * mm});
            skLineSegment(sketch, "E132.0.3.6", {"start": v(-2433.27, -137) * mm, "end": v(-2433.27, -169.52) * mm});
            skLineSegment(sketch, "E132.0.3.7", {"start": v(-2360.88, -137) * mm, "end": v(-2360.88, -169.52) * mm});
            skLineSegment(sketch, "E132.0.3.8", {"start": v(-2113.36, -137) * mm, "end": v(-2113.36, -169.52) * mm});
            skLineSegment(sketch, "E132.0.3.9", {"start": v(-2216.1, -169.52) * mm, "end": v(-2185.75, -169.52) * mm});
            skLineSegment(sketch, "E132.0.3.10", {"start": v(-2288.5, -137) * mm, "end": v(-2288.5, -169.52) * mm});
            skLineSegment(sketch, "E132.0.3.11", {"start": v(-2143.71, -169.52) * mm, "end": v(-2113.36, -169.52) * mm});
            skLineSegment(sketch, "E132.0.3.12", {"start": v(-2433.27, -169.52) * mm, "end": v(-2402.92, -169.52) * mm});
            skLineSegment(sketch, "E132.0.3.13", {"start": v(-2402.92, -137) * mm, "end": v(-2402.92, -169.52) * mm});
            skLineSegment(sketch, "E132.0.3.14", {"start": v(-2433.27, -137) * mm, "end": v(-2360.88, -137) * mm, "construction": true});
            skLineSegment(sketch, "E132.0.3.15", {"start": v(-2360.88, -137) * mm, "end": v(-2330.53, -137) * mm});
            skLineSegment(sketch, "E132.0.3.16", {"start": v(-2360.88, -169.52) * mm, "end": v(-2330.53, -169.52) * mm});
            skLineSegment(sketch, "E132.0.3.17", {"start": v(-2216.1, -137) * mm, "end": v(-2185.75, -137) * mm});
            skLineSegment(sketch, "E132.0.3.18", {"start": v(-2143.71, -137) * mm, "end": v(-2113.36, -137) * mm});
            skLineSegment(sketch, "E132.0.3.19", {"start": v(-2330.53, -137) * mm, "end": v(-2330.53, -169.52) * mm});
            skLineSegment(sketch, "E132.0.3.20", {"start": v(-2433.27, -137) * mm, "end": v(-2402.92, -137) * mm});
            skLineSegment(sketch, "E132.0.4.0", {"start": v(-2143.71, -228) * mm, "end": v(-2143.71, -260.52) * mm});
            skLineSegment(sketch, "E132.0.4.1", {"start": v(-2288.5, -260.52) * mm, "end": v(-2258.14, -260.52) * mm});
            skLineSegment(sketch, "E132.0.4.2", {"start": v(-2288.5, -228) * mm, "end": v(-2258.14, -228) * mm});
            skLineSegment(sketch, "E132.0.4.3", {"start": v(-2185.75, -228) * mm, "end": v(-2185.75, -260.52) * mm});
            skLineSegment(sketch, "E132.0.4.4", {"start": v(-2258.14, -228) * mm, "end": v(-2258.14, -260.52) * mm});
            skLineSegment(sketch, "E132.0.4.5", {"start": v(-2216.1, -228) * mm, "end": v(-2216.1, -260.52) * mm});
            skLineSegment(sketch, "E132.0.4.8", {"start": v(-2113.36, -228) * mm, "end": v(-2113.36, -260.52) * mm});
            skLineSegment(sketch, "E132.0.4.9", {"start": v(-2216.1, -260.52) * mm, "end": v(-2185.75, -260.52) * mm});
            skLineSegment(sketch, "E132.0.4.10", {"start": v(-2288.5, -228) * mm, "end": v(-2288.5, -260.52) * mm});
            skLineSegment(sketch, "E132.0.4.11", {"start": v(-2143.71, -260.52) * mm, "end": v(-2113.36, -260.52) * mm});
            skLineSegment(sketch, "E132.0.4.17", {"start": v(-2216.1, -228) * mm, "end": v(-2185.75, -228) * mm});
            skLineSegment(sketch, "E132.0.4.18", {"start": v(-2143.71, -228) * mm, "end": v(-2113.36, -228) * mm});
            skLineSegment(sketch, "E132.0.5.0", {"start": v(-2143.71, -319) * mm, "end": v(-2143.71, -351.52) * mm});
            skLineSegment(sketch, "E132.0.5.1", {"start": v(-2288.5, -351.52) * mm, "end": v(-2258.14, -351.52) * mm});
            skLineSegment(sketch, "E132.0.5.2", {"start": v(-2288.5, -319) * mm, "end": v(-2258.14, -319) * mm});
            skLineSegment(sketch, "E132.0.5.3", {"start": v(-2185.75, -319) * mm, "end": v(-2185.75, -351.52) * mm});
            skLineSegment(sketch, "E132.0.5.4", {"start": v(-2258.14, -319) * mm, "end": v(-2258.14, -351.52) * mm});
            skLineSegment(sketch, "E132.0.5.5", {"start": v(-2216.1, -319) * mm, "end": v(-2216.1, -351.52) * mm});
            skLineSegment(sketch, "E132.0.5.6", {"start": v(-2433.27, -319) * mm, "end": v(-2433.27, -351.52) * mm});
            skLineSegment(sketch, "E132.0.5.7", {"start": v(-2360.88, -319) * mm, "end": v(-2360.88, -351.52) * mm});
            skLineSegment(sketch, "E132.0.5.8", {"start": v(-2113.36, -319) * mm, "end": v(-2113.36, -351.52) * mm});
            skLineSegment(sketch, "E132.0.5.9", {"start": v(-2216.1, -351.52) * mm, "end": v(-2185.75, -351.52) * mm});
            skLineSegment(sketch, "E132.0.5.10", {"start": v(-2288.5, -319) * mm, "end": v(-2288.5, -351.52) * mm});
            skLineSegment(sketch, "E132.0.5.11", {"start": v(-2143.71, -351.52) * mm, "end": v(-2113.36, -351.52) * mm});
            skLineSegment(sketch, "E132.0.5.12", {"start": v(-2433.27, -351.52) * mm, "end": v(-2402.92, -351.52) * mm});
            skLineSegment(sketch, "E132.0.5.13", {"start": v(-2402.92, -319) * mm, "end": v(-2402.92, -351.52) * mm});
            skLineSegment(sketch, "E132.0.5.14", {"start": v(-2433.27, -319) * mm, "end": v(-2360.88, -319) * mm, "construction": true});
            skLineSegment(sketch, "E132.0.5.15", {"start": v(-2360.88, -319) * mm, "end": v(-2330.53, -319) * mm});
            skLineSegment(sketch, "E132.0.5.16", {"start": v(-2360.88, -351.52) * mm, "end": v(-2330.53, -351.52) * mm});
            skLineSegment(sketch, "E132.0.5.17", {"start": v(-2216.1, -319) * mm, "end": v(-2185.75, -319) * mm});
            skLineSegment(sketch, "E132.0.5.18", {"start": v(-2143.71, -319) * mm, "end": v(-2113.36, -319) * mm});
            skLineSegment(sketch, "E132.0.5.19", {"start": v(-2330.53, -319) * mm, "end": v(-2330.53, -351.52) * mm});
            skLineSegment(sketch, "E132.0.5.20", {"start": v(-2433.27, -319) * mm, "end": v(-2402.92, -319) * mm});
            skLineSegment(sketch, "E132.0.6.0", {"start": v(-2143.71, -410) * mm, "end": v(-2143.71, -442.52) * mm});
            skLineSegment(sketch, "E132.0.6.3", {"start": v(-2185.75, -410) * mm, "end": v(-2185.75, -442.52) * mm});
            skLineSegment(sketch, "E132.0.6.5", {"start": v(-2216.1, -410) * mm, "end": v(-2216.1, -442.52) * mm});
            skLineSegment(sketch, "E132.0.6.6", {"start": v(-2433.27, -410) * mm, "end": v(-2433.27, -442.52) * mm});
            skLineSegment(sketch, "E132.0.6.7", {"start": v(-2360.88, -410) * mm, "end": v(-2360.88, -442.52) * mm});
            skLineSegment(sketch, "E132.0.6.8", {"start": v(-2113.36, -410) * mm, "end": v(-2113.36, -442.52) * mm});
            skLineSegment(sketch, "E132.0.6.9", {"start": v(-2216.1, -442.52) * mm, "end": v(-2185.75, -442.52) * mm});
            skLineSegment(sketch, "E132.0.6.11", {"start": v(-2143.71, -442.52) * mm, "end": v(-2113.36, -442.52) * mm});
            skLineSegment(sketch, "E132.0.6.12", {"start": v(-2433.27, -442.52) * mm, "end": v(-2402.92, -442.52) * mm});
            skLineSegment(sketch, "E132.0.6.13", {"start": v(-2402.92, -410) * mm, "end": v(-2402.92, -442.52) * mm});
            skLineSegment(sketch, "E132.0.6.14", {"start": v(-2433.27, -410) * mm, "end": v(-2360.88, -410) * mm, "construction": true});
            skLineSegment(sketch, "E132.0.6.15", {"start": v(-2360.88, -410) * mm, "end": v(-2330.53, -410) * mm});
            skLineSegment(sketch, "E132.0.6.16", {"start": v(-2360.88, -442.52) * mm, "end": v(-2330.53, -442.52) * mm});
            skLineSegment(sketch, "E132.0.6.17", {"start": v(-2216.1, -410) * mm, "end": v(-2185.75, -410) * mm});
            skLineSegment(sketch, "E132.0.6.18", {"start": v(-2143.71, -410) * mm, "end": v(-2113.36, -410) * mm});
            skLineSegment(sketch, "E132.0.6.19", {"start": v(-2330.53, -410) * mm, "end": v(-2330.53, -442.52) * mm});
            skLineSegment(sketch, "E132.0.6.20", {"start": v(-2433.27, -410) * mm, "end": v(-2402.92, -410) * mm});
            skLineSegment(sketch, "E132.0.7.0", {"start": v(-2143.71, -501) * mm, "end": v(-2143.71, -533.52) * mm});
            skLineSegment(sketch, "E132.0.7.1", {"start": v(-2288.5, -533.52) * mm, "end": v(-2258.14, -533.52) * mm});
            skLineSegment(sketch, "E132.0.7.2", {"start": v(-2288.5, -501) * mm, "end": v(-2258.14, -501) * mm});
            skLineSegment(sketch, "E132.0.7.3", {"start": v(-2185.75, -501) * mm, "end": v(-2185.75, -533.52) * mm});
            skLineSegment(sketch, "E132.0.7.4", {"start": v(-2258.14, -501) * mm, "end": v(-2258.14, -533.52) * mm});
            skLineSegment(sketch, "E132.0.7.5", {"start": v(-2216.1, -501) * mm, "end": v(-2216.1, -533.52) * mm});
            skLineSegment(sketch, "E132.0.7.6", {"start": v(-2433.27, -501) * mm, "end": v(-2433.27, -533.52) * mm});
            skLineSegment(sketch, "E132.0.7.7", {"start": v(-2360.88, -501) * mm, "end": v(-2360.88, -533.52) * mm});
            skLineSegment(sketch, "E132.0.7.8", {"start": v(-2113.36, -501) * mm, "end": v(-2113.36, -533.52) * mm});
            skLineSegment(sketch, "E132.0.7.9", {"start": v(-2216.1, -533.52) * mm, "end": v(-2185.75, -533.52) * mm});
            skLineSegment(sketch, "E132.0.7.10", {"start": v(-2288.5, -501) * mm, "end": v(-2288.5, -533.52) * mm});
            skLineSegment(sketch, "E132.0.7.11", {"start": v(-2143.71, -533.52) * mm, "end": v(-2113.36, -533.52) * mm});
            skLineSegment(sketch, "E132.0.7.12", {"start": v(-2433.27, -533.52) * mm, "end": v(-2402.92, -533.52) * mm});
            skLineSegment(sketch, "E132.0.7.13", {"start": v(-2402.92, -501) * mm, "end": v(-2402.92, -533.52) * mm});
            skLineSegment(sketch, "E132.0.7.14", {"start": v(-2433.27, -501) * mm, "end": v(-2360.88, -501) * mm, "construction": true});
            skLineSegment(sketch, "E132.0.7.15", {"start": v(-2360.88, -501) * mm, "end": v(-2330.53, -501) * mm});
            skLineSegment(sketch, "E132.0.7.16", {"start": v(-2360.88, -533.52) * mm, "end": v(-2330.53, -533.52) * mm});
            skLineSegment(sketch, "E132.0.7.17", {"start": v(-2216.1, -501) * mm, "end": v(-2185.75, -501) * mm});
            skLineSegment(sketch, "E132.0.7.18", {"start": v(-2143.71, -501) * mm, "end": v(-2113.36, -501) * mm});
            skLineSegment(sketch, "E132.0.7.19", {"start": v(-2330.53, -501) * mm, "end": v(-2330.53, -533.52) * mm});
            skLineSegment(sketch, "E132.0.7.20", {"start": v(-2433.27, -501) * mm, "end": v(-2402.92, -501) * mm});
            skLineSegment(sketch, "E132.direction1", {"start": v(-2433.27, 103.48) * mm, "end": v(-2408.27, 103.48) * mm, "construction": true});
            skLineSegment(sketch, "E132.direction2", {"start": v(-2433.27, 103.48) * mm, "end": v(-2433.27, 12.48) * mm, "construction": true});
            skLineSegment(sketch, "E133.bottom", {"start": v(-3724.48, 147.2) * mm, "end": v(-3618.43, 147.2) * mm});
            skLineSegment(sketch, "E133.top", {"start": v(-3724.48, 94.18) * mm, "end": v(-3618.43, 94.18) * mm});
            skLineSegment(sketch, "E133.left", {"start": v(-3724.48, 147.2) * mm, "end": v(-3724.48, 94.18) * mm});
            skLineSegment(sketch, "E133.right", {"start": v(-3618.43, 147.2) * mm, "end": v(-3618.43, 94.18) * mm});
            skLineSegment(sketch, "E134.bottom", {"start": v(-3464.34, 696.14) * mm, "end": v(-3358.28, 696.14) * mm});
            skLineSegment(sketch, "E134.top", {"start": v(-3464.34, 643.11) * mm, "end": v(-3358.28, 643.11) * mm});
            skLineSegment(sketch, "E134.left", {"start": v(-3464.34, 696.14) * mm, "end": v(-3464.34, 643.11) * mm});
            skLineSegment(sketch, "E134.right", {"start": v(-3358.28, 696.14) * mm, "end": v(-3358.28, 643.11) * mm});
            skLineSegment(sketch, "E135.bottom", {"start": v(-3464.34, 627.2) * mm, "end": v(-3358.28, 627.2) * mm});
            skLineSegment(sketch, "E135.top", {"start": v(-3464.34, 574.18) * mm, "end": v(-3358.28, 574.18) * mm});
            skLineSegment(sketch, "E135.left", {"start": v(-3464.34, 627.2) * mm, "end": v(-3464.34, 574.18) * mm});
            skLineSegment(sketch, "E135.right", {"start": v(-3358.28, 627.2) * mm, "end": v(-3358.28, 574.18) * mm});
            skLineSegment(sketch, "E136.bottom", {"start": v(-3596.32, 150.06) * mm, "end": v(-3489.62, 150.06) * mm});
            skLineSegment(sketch, "E136.top", {"start": v(-3596.32, 94.18) * mm, "end": v(-3489.62, 94.18) * mm});
            skLineSegment(sketch, "E136.left", {"start": v(-3596.32, 150.06) * mm, "end": v(-3596.32, 94.18) * mm});
            skLineSegment(sketch, "E136.right", {"start": v(-3489.62, 150.06) * mm, "end": v(-3489.62, 94.18) * mm});
            skLineSegment(sketch, "E137.0.1.0", {"start": v(-3464.34, 531.2) * mm, "end": v(-3358.28, 531.2) * mm});
            skLineSegment(sketch, "E137.0.1.1", {"start": v(-3464.34, 531.2) * mm, "end": v(-3464.34, 478.18) * mm});
            skLineSegment(sketch, "E137.0.1.2", {"start": v(-3464.34, 478.18) * mm, "end": v(-3358.28, 478.18) * mm});
            skLineSegment(sketch, "E137.0.1.3", {"start": v(-3358.28, 531.2) * mm, "end": v(-3358.28, 478.18) * mm});
            skLineSegment(sketch, "E137.0.3.0", {"start": v(-3464.34, 339.2) * mm, "end": v(-3358.28, 339.2) * mm});
            skLineSegment(sketch, "E137.0.3.1", {"start": v(-3464.34, 339.2) * mm, "end": v(-3464.34, 286.18) * mm});
            skLineSegment(sketch, "E137.0.3.2", {"start": v(-3464.34, 286.18) * mm, "end": v(-3358.28, 286.18) * mm});
            skLineSegment(sketch, "E137.0.3.3", {"start": v(-3358.28, 339.2) * mm, "end": v(-3358.28, 286.18) * mm});
            skLineSegment(sketch, "E137.0.4.0", {"start": v(-3464.34, 243.2) * mm, "end": v(-3358.28, 243.2) * mm});
            skLineSegment(sketch, "E137.0.4.1", {"start": v(-3464.34, 243.2) * mm, "end": v(-3464.34, 190.18) * mm});
            skLineSegment(sketch, "E137.0.4.2", {"start": v(-3464.34, 190.18) * mm, "end": v(-3358.28, 190.18) * mm});
            skLineSegment(sketch, "E137.0.4.3", {"start": v(-3358.28, 243.2) * mm, "end": v(-3358.28, 190.18) * mm});
            skLineSegment(sketch, "E137.0.5.0", {"start": v(-3464.34, 147.2) * mm, "end": v(-3358.28, 147.2) * mm});
            skLineSegment(sketch, "E137.0.5.1", {"start": v(-3464.34, 147.2) * mm, "end": v(-3464.34, 94.18) * mm});
            skLineSegment(sketch, "E137.0.5.2", {"start": v(-3464.34, 94.18) * mm, "end": v(-3358.28, 94.18) * mm});
            skLineSegment(sketch, "E137.0.5.3", {"start": v(-3358.28, 147.2) * mm, "end": v(-3358.28, 94.18) * mm});
            skLineSegment(sketch, "E137.0.6.0", {"start": v(-3464.34, 51.2) * mm, "end": v(-3358.28, 51.2) * mm});
            skLineSegment(sketch, "E137.0.6.1", {"start": v(-3464.34, 51.2) * mm, "end": v(-3464.34, -1.82) * mm});
            skLineSegment(sketch, "E137.0.6.2", {"start": v(-3464.34, -1.82) * mm, "end": v(-3358.28, -1.82) * mm});
            skLineSegment(sketch, "E137.0.6.3", {"start": v(-3358.28, 51.2) * mm, "end": v(-3358.28, -1.82) * mm});
            skLineSegment(sketch, "E137.0.7.0", {"start": v(-3464.34, -44.8) * mm, "end": v(-3358.28, -44.8) * mm});
            skLineSegment(sketch, "E137.0.7.1", {"start": v(-3464.34, -44.8) * mm, "end": v(-3464.34, -97.82) * mm});
            skLineSegment(sketch, "E137.0.7.2", {"start": v(-3464.34, -97.82) * mm, "end": v(-3358.28, -97.82) * mm});
            skLineSegment(sketch, "E137.0.7.3", {"start": v(-3358.28, -44.8) * mm, "end": v(-3358.28, -97.82) * mm});
            skLineSegment(sketch, "E137.0.9.0", {"start": v(-3464.34, -236.8) * mm, "end": v(-3358.28, -236.8) * mm});
            skLineSegment(sketch, "E137.0.9.1", {"start": v(-3464.34, -236.8) * mm, "end": v(-3464.34, -289.82) * mm});
            skLineSegment(sketch, "E137.0.9.2", {"start": v(-3464.34, -289.82) * mm, "end": v(-3358.28, -289.82) * mm});
            skLineSegment(sketch, "E137.0.9.3", {"start": v(-3358.28, -236.8) * mm, "end": v(-3358.28, -289.82) * mm});
            skLineSegment(sketch, "E137.0.10.0", {"start": v(-3464.34, -332.8) * mm, "end": v(-3358.28, -332.8) * mm});
            skLineSegment(sketch, "E137.0.10.1", {"start": v(-3464.34, -332.8) * mm, "end": v(-3464.34, -385.82) * mm});
            skLineSegment(sketch, "E137.0.10.2", {"start": v(-3464.34, -385.82) * mm, "end": v(-3358.28, -385.82) * mm});
            skLineSegment(sketch, "E137.0.10.3", {"start": v(-3358.28, -332.8) * mm, "end": v(-3358.28, -385.82) * mm});
            skLineSegment(sketch, "E137.0.11.0", {"start": v(-3464.34, -428.8) * mm, "end": v(-3358.28, -428.8) * mm});
            skLineSegment(sketch, "E137.0.11.1", {"start": v(-3464.34, -428.8) * mm, "end": v(-3464.34, -481.82) * mm});
            skLineSegment(sketch, "E137.0.11.2", {"start": v(-3464.34, -481.82) * mm, "end": v(-3358.28, -481.82) * mm});
            skLineSegment(sketch, "E137.0.11.3", {"start": v(-3358.28, -428.8) * mm, "end": v(-3358.28, -481.82) * mm});
            skLineSegment(sketch, "E137.0.12.0", {"start": v(-3464.34, -524.8) * mm, "end": v(-3358.28, -524.8) * mm});
            skLineSegment(sketch, "E137.0.12.1", {"start": v(-3464.34, -524.8) * mm, "end": v(-3464.34, -577.82) * mm});
            skLineSegment(sketch, "E137.0.12.2", {"start": v(-3464.34, -577.82) * mm, "end": v(-3358.28, -577.82) * mm});
            skLineSegment(sketch, "E137.0.12.3", {"start": v(-3358.28, -524.8) * mm, "end": v(-3358.28, -577.82) * mm});
            skLineSegment(sketch, "E137.0.13.0", {"start": v(-3464.34, -620.8) * mm, "end": v(-3358.28, -620.8) * mm});
            skLineSegment(sketch, "E137.0.13.1", {"start": v(-3464.34, -620.8) * mm, "end": v(-3464.34, -673.82) * mm});
            skLineSegment(sketch, "E137.0.13.2", {"start": v(-3464.34, -673.82) * mm, "end": v(-3358.28, -673.82) * mm});
            skLineSegment(sketch, "E137.0.13.3", {"start": v(-3358.28, -620.8) * mm, "end": v(-3358.28, -673.82) * mm});
            skLineSegment(sketch, "E137.direction1", {"start": v(-3464.34, 574.18) * mm, "end": v(-3439.34, 574.18) * mm, "construction": true});
            skLineSegment(sketch, "E137.direction2", {"start": v(-3464.34, 574.18) * mm, "end": v(-3464.34, 478.18) * mm, "construction": true});
            skLineSegment(sketch, "E138.0.1.0", {"start": v(-3618.43, 51.2) * mm, "end": v(-3618.43, -1.82) * mm});
            skLineSegment(sketch, "E138.0.1.1", {"start": v(-3724.48, 51.2) * mm, "end": v(-3724.48, -1.82) * mm});
            skLineSegment(sketch, "E138.0.1.6", {"start": v(-3724.48, 51.2) * mm, "end": v(-3618.43, 51.2) * mm});
            skLineSegment(sketch, "E138.0.1.7", {"start": v(-3724.48, -1.82) * mm, "end": v(-3618.43, -1.82) * mm});
            skLineSegment(sketch, "E138.0.2.0", {"start": v(-3618.43, -44.8) * mm, "end": v(-3618.43, -97.82) * mm});
            skLineSegment(sketch, "E138.0.2.1", {"start": v(-3724.48, -44.8) * mm, "end": v(-3724.48, -97.82) * mm});
            skLineSegment(sketch, "E138.0.2.2", {"start": v(-3596.32, -41.94) * mm, "end": v(-3489.62, -41.94) * mm});
            skLineSegment(sketch, "E138.0.2.3", {"start": v(-3596.32, -97.82) * mm, "end": v(-3489.62, -97.82) * mm});
            skLineSegment(sketch, "E138.0.2.4", {"start": v(-3596.32, -41.94) * mm, "end": v(-3596.32, -97.82) * mm});
            skLineSegment(sketch, "E138.0.2.5", {"start": v(-3489.62, -41.94) * mm, "end": v(-3489.62, -97.82) * mm});
            skLineSegment(sketch, "E138.0.2.6", {"start": v(-3724.48, -44.8) * mm, "end": v(-3618.43, -44.8) * mm});
            skLineSegment(sketch, "E138.0.2.7", {"start": v(-3724.48, -97.82) * mm, "end": v(-3618.43, -97.82) * mm});
            skLineSegment(sketch, "E138.0.3.0", {"start": v(-3618.43, -140.8) * mm, "end": v(-3618.43, -193.82) * mm});
            skLineSegment(sketch, "E138.0.3.1", {"start": v(-3724.48, -140.8) * mm, "end": v(-3724.48, -193.82) * mm});
            skLineSegment(sketch, "E138.0.3.2", {"start": v(-3596.32, -137.94) * mm, "end": v(-3489.62, -137.94) * mm});
            skLineSegment(sketch, "E138.0.3.3", {"start": v(-3596.32, -193.82) * mm, "end": v(-3489.62, -193.82) * mm});
            skLineSegment(sketch, "E138.0.3.4", {"start": v(-3596.32, -137.94) * mm, "end": v(-3596.32, -193.82) * mm});
            skLineSegment(sketch, "E138.0.3.5", {"start": v(-3489.62, -137.94) * mm, "end": v(-3489.62, -193.82) * mm});
            skLineSegment(sketch, "E138.0.3.6", {"start": v(-3724.48, -140.8) * mm, "end": v(-3618.43, -140.8) * mm});
            skLineSegment(sketch, "E138.0.3.7", {"start": v(-3724.48, -193.82) * mm, "end": v(-3618.43, -193.82) * mm});
            skLineSegment(sketch, "E138.0.4.2", {"start": v(-3596.32, -233.94) * mm, "end": v(-3489.62, -233.94) * mm});
            skLineSegment(sketch, "E138.0.4.3", {"start": v(-3596.32, -289.82) * mm, "end": v(-3489.62, -289.82) * mm});
            skLineSegment(sketch, "E138.0.4.4", {"start": v(-3596.32, -233.94) * mm, "end": v(-3596.32, -289.82) * mm});
            skLineSegment(sketch, "E138.0.4.5", {"start": v(-3489.62, -233.94) * mm, "end": v(-3489.62, -289.82) * mm});
            skLineSegment(sketch, "E138.0.5.0", {"start": v(-3618.43, -332.8) * mm, "end": v(-3618.43, -385.82) * mm});
            skLineSegment(sketch, "E138.0.5.1", {"start": v(-3724.48, -332.8) * mm, "end": v(-3724.48, -385.82) * mm});
            skLineSegment(sketch, "E138.0.5.2", {"start": v(-3596.32, -329.94) * mm, "end": v(-3489.62, -329.94) * mm});
            skLineSegment(sketch, "E138.0.5.3", {"start": v(-3596.32, -385.82) * mm, "end": v(-3489.62, -385.82) * mm});
            skLineSegment(sketch, "E138.0.5.4", {"start": v(-3596.32, -329.94) * mm, "end": v(-3596.32, -385.82) * mm});
            skLineSegment(sketch, "E138.0.5.5", {"start": v(-3489.62, -329.94) * mm, "end": v(-3489.62, -385.82) * mm});
            skLineSegment(sketch, "E138.0.5.6", {"start": v(-3724.48, -332.8) * mm, "end": v(-3618.43, -332.8) * mm});
            skLineSegment(sketch, "E138.0.5.7", {"start": v(-3724.48, -385.82) * mm, "end": v(-3618.43, -385.82) * mm});
            skLineSegment(sketch, "E138.direction1", {"start": v(-3724.48, 94.18) * mm, "end": v(-3699.48, 94.18) * mm, "construction": true});
            skLineSegment(sketch, "E138.direction2", {"start": v(-3724.48, 94.18) * mm, "end": v(-3724.48, -1.82) * mm, "construction": true});
            skLineSegment(sketch, "E139.bottom", {"start": v(893.4, 666.48) * mm, "end": v(1143.33, 666.48) * mm});
            skLineSegment(sketch, "E139.top", {"start": v(893.4, 629.36) * mm, "end": v(1143.33, 629.36) * mm});
            skLineSegment(sketch, "E139.left", {"start": v(893.4, 666.48) * mm, "end": v(893.4, 629.36) * mm});
            skLineSegment(sketch, "E139.right", {"start": v(1143.33, 666.48) * mm, "end": v(1143.33, 629.36) * mm});
            skLineSegment(sketch, "E140.0.1.0", {"start": v(893.4, 455.36) * mm, "end": v(1143.33, 455.36) * mm});
            skLineSegment(sketch, "E140.0.1.1", {"start": v(893.4, 492.48) * mm, "end": v(1143.33, 492.48) * mm});
            skLineSegment(sketch, "E140.0.1.2", {"start": v(1143.33, 492.48) * mm, "end": v(1143.33, 455.36) * mm});
            skLineSegment(sketch, "E140.0.1.3", {"start": v(893.4, 492.48) * mm, "end": v(893.4, 455.36) * mm});
            skLineSegment(sketch, "E140.0.2.0", {"start": v(893.4, 281.36) * mm, "end": v(1143.33, 281.36) * mm});
            skLineSegment(sketch, "E140.0.2.1", {"start": v(893.4, 318.48) * mm, "end": v(1143.33, 318.48) * mm});
            skLineSegment(sketch, "E140.0.2.2", {"start": v(1143.33, 318.48) * mm, "end": v(1143.33, 281.36) * mm});
            skLineSegment(sketch, "E140.0.2.3", {"start": v(893.4, 318.48) * mm, "end": v(893.4, 281.36) * mm});
            skLineSegment(sketch, "E140.0.3.0", {"start": v(893.4, 107.36) * mm, "end": v(1143.33, 107.36) * mm});
            skLineSegment(sketch, "E140.0.3.1", {"start": v(893.4, 144.48) * mm, "end": v(1143.33, 144.48) * mm});
            skLineSegment(sketch, "E140.0.3.2", {"start": v(1143.33, 144.48) * mm, "end": v(1143.33, 107.36) * mm});
            skLineSegment(sketch, "E140.0.3.3", {"start": v(893.4, 144.48) * mm, "end": v(893.4, 107.36) * mm});
            skLineSegment(sketch, "E140.0.4.0", {"start": v(893.4, -66.64) * mm, "end": v(1143.33, -66.64) * mm});
            skLineSegment(sketch, "E140.0.4.1", {"start": v(893.4, -29.52) * mm, "end": v(1143.33, -29.52) * mm});
            skLineSegment(sketch, "E140.0.4.2", {"start": v(1143.33, -29.52) * mm, "end": v(1143.33, -66.64) * mm});
            skLineSegment(sketch, "E140.0.4.3", {"start": v(893.4, -29.52) * mm, "end": v(893.4, -66.64) * mm});
            skLineSegment(sketch, "E140.0.5.0", {"start": v(893.4, -240.64) * mm, "end": v(1143.33, -240.64) * mm});
            skLineSegment(sketch, "E140.0.5.1", {"start": v(893.4, -203.52) * mm, "end": v(1143.33, -203.52) * mm});
            skLineSegment(sketch, "E140.0.5.2", {"start": v(1143.33, -203.52) * mm, "end": v(1143.33, -240.64) * mm});
            skLineSegment(sketch, "E140.0.5.3", {"start": v(893.4, -203.52) * mm, "end": v(893.4, -240.64) * mm});
            skLineSegment(sketch, "E140.0.6.0", {"start": v(893.4, -414.64) * mm, "end": v(1143.33, -414.64) * mm});
            skLineSegment(sketch, "E140.0.6.1", {"start": v(893.4, -377.52) * mm, "end": v(1143.33, -377.52) * mm});
            skLineSegment(sketch, "E140.0.6.2", {"start": v(1143.33, -377.52) * mm, "end": v(1143.33, -414.64) * mm});
            skLineSegment(sketch, "E140.0.6.3", {"start": v(893.4, -377.52) * mm, "end": v(893.4, -414.64) * mm});
            skLineSegment(sketch, "E140.direction1", {"start": v(893.4, 629.36) * mm, "end": v(918.4, 629.36) * mm, "construction": true});
            skLineSegment(sketch, "E140.direction2", {"start": v(893.4, 629.36) * mm, "end": v(893.4, 455.36) * mm, "construction": true});
            skLineSegment(sketch, "E141.bottom", {"start": v(1229.48, 358.7) * mm, "end": v(1295.02, 358.7) * mm});
            skLineSegment(sketch, "E141.top", {"start": v(1229.48, 177.81) * mm, "end": v(1295.02, 177.81) * mm});
            skLineSegment(sketch, "E141.left", {"start": v(1229.48, 358.7) * mm, "end": v(1229.48, 177.81) * mm});
            skLineSegment(sketch, "E141.right", {"start": v(1295.02, 358.7) * mm, "end": v(1295.02, 177.81) * mm});
            skLineSegment(sketch, "E142.0.1.0", {"start": v(1229.48, 123.7) * mm, "end": v(1295.02, 123.7) * mm});
            skLineSegment(sketch, "E142.0.1.1", {"start": v(1229.48, 123.7) * mm, "end": v(1229.48, -57.19) * mm});
            skLineSegment(sketch, "E142.0.1.2", {"start": v(1295.02, 123.7) * mm, "end": v(1295.02, -57.19) * mm});
            skLineSegment(sketch, "E142.0.1.3", {"start": v(1229.48, -57.19) * mm, "end": v(1295.02, -57.19) * mm});
            skLineSegment(sketch, "E142.0.2.0", {"start": v(1229.48, -111.3) * mm, "end": v(1295.02, -111.3) * mm});
            skLineSegment(sketch, "E142.0.2.1", {"start": v(1229.48, -111.3) * mm, "end": v(1229.48, -292.19) * mm});
            skLineSegment(sketch, "E142.0.2.2", {"start": v(1295.02, -111.3) * mm, "end": v(1295.02, -292.19) * mm});
            skLineSegment(sketch, "E142.0.2.3", {"start": v(1229.48, -292.19) * mm, "end": v(1295.02, -292.19) * mm});
            skLineSegment(sketch, "E142.0.3.0", {"start": v(1229.48, -346.3) * mm, "end": v(1295.02, -346.3) * mm});
            skLineSegment(sketch, "E142.0.3.1", {"start": v(1229.48, -346.3) * mm, "end": v(1229.48, -527.19) * mm});
            skLineSegment(sketch, "E142.0.3.2", {"start": v(1295.02, -346.3) * mm, "end": v(1295.02, -527.19) * mm});
            skLineSegment(sketch, "E142.0.3.3", {"start": v(1229.48, -527.19) * mm, "end": v(1295.02, -527.19) * mm});
            skLineSegment(sketch, "E142.1.0.0", {"start": v(1364.48, 358.7) * mm, "end": v(1430.02, 358.7) * mm});
            skLineSegment(sketch, "E142.1.0.1", {"start": v(1364.48, 358.7) * mm, "end": v(1364.48, 177.81) * mm});
            skLineSegment(sketch, "E142.1.0.2", {"start": v(1430.02, 358.7) * mm, "end": v(1430.02, 177.81) * mm});
            skLineSegment(sketch, "E142.1.0.3", {"start": v(1364.48, 177.81) * mm, "end": v(1430.02, 177.81) * mm});
            skLineSegment(sketch, "E142.1.1.0", {"start": v(1364.48, 123.7) * mm, "end": v(1430.02, 123.7) * mm});
            skLineSegment(sketch, "E142.1.1.1", {"start": v(1364.48, 123.7) * mm, "end": v(1364.48, -57.19) * mm});
            skLineSegment(sketch, "E142.1.1.2", {"start": v(1430.02, 123.7) * mm, "end": v(1430.02, -57.19) * mm});
            skLineSegment(sketch, "E142.1.1.3", {"start": v(1364.48, -57.19) * mm, "end": v(1430.02, -57.19) * mm});
            skLineSegment(sketch, "E142.1.2.0", {"start": v(1364.48, -111.3) * mm, "end": v(1430.02, -111.3) * mm});
            skLineSegment(sketch, "E142.1.2.1", {"start": v(1364.48, -111.3) * mm, "end": v(1364.48, -292.19) * mm});
            skLineSegment(sketch, "E142.1.2.2", {"start": v(1430.02, -111.3) * mm, "end": v(1430.02, -292.19) * mm});
            skLineSegment(sketch, "E142.1.2.3", {"start": v(1364.48, -292.19) * mm, "end": v(1430.02, -292.19) * mm});
            skLineSegment(sketch, "E142.1.3.0", {"start": v(1364.48, -346.3) * mm, "end": v(1430.02, -346.3) * mm});
            skLineSegment(sketch, "E142.1.3.1", {"start": v(1364.48, -346.3) * mm, "end": v(1364.48, -527.19) * mm});
            skLineSegment(sketch, "E142.1.3.2", {"start": v(1430.02, -346.3) * mm, "end": v(1430.02, -527.19) * mm});
            skLineSegment(sketch, "E142.1.3.3", {"start": v(1364.48, -527.19) * mm, "end": v(1430.02, -527.19) * mm});
            skLineSegment(sketch, "E142.direction1", {"start": v(1229.48, 358.7) * mm, "end": v(1364.48, 358.7) * mm, "construction": true});
            skLineSegment(sketch, "E142.direction2", {"start": v(1229.48, 358.7) * mm, "end": v(1229.48, 123.7) * mm, "construction": true});
            skLineSegment(sketch, "E143.bottom", {"start": v(365.16, -503.86) * mm, "end": v(593.25, -503.86) * mm});
            skLineSegment(sketch, "E144.bottom", {"start": v(341.71, -745.5) * mm, "end": v(616.7, -745.5) * mm});
            skLineSegment(sketch, "E144.top", {"start": v(341.71, -823.15) * mm, "end": v(616.7, -823.15) * mm});
            skLineSegment(sketch, "E144.left", {"start": v(341.71, -745.5) * mm, "end": v(341.71, -776.06) * mm});
            skLineSegment(sketch, "E144.right", {"start": v(616.7, -745.5) * mm, "end": v(616.7, -776.06) * mm});
            skLineSegment(sketch, "E145.bottom", {"start": v(341.71, -776.06) * mm, "end": v(616.7, -776.06) * mm});
            skLineSegment(sketch, "E145.top", {"start": v(338.94, -823.15) * mm, "end": v(616.7, -823.15) * mm});
            skLineSegment(sketch, "E146", {"start": v(341.71, -776.06) * mm, "end": v(302.6, -776.06) * mm});
            skLineSegment(sketch, "E147", {"start": v(302.6, -776.06) * mm, "end": v(300.77, -823.15) * mm});
            skLineSegment(sketch, "E148", {"start": v(479.2, -745.5) * mm, "end": v(479.2, -823.15) * mm, "construction": true});
            skLineSegment(sketch, "E149.MirrorCS", {"start": v(655.8, -776.06) * mm, "end": v(657.64, -823.15) * mm});
            skLineSegment(sketch, "E150.MirrorCS", {"start": v(616.7, -776.06) * mm, "end": v(655.8, -776.06) * mm});
            skLineSegment(sketch, "E151", {"start": v(365.16, -745.5) * mm, "end": v(365.16, -503.86) * mm});
            skLineSegment(sketch, "E152.MirrorCS", {"start": v(593.25, -745.5) * mm, "end": v(593.25, -503.86) * mm});
            skPoint(sketch, "E153.orphan", {"position": v(593.25, -504.17) * mm});
            skPoint(sketch, "E154.orphan", {"position": v(365.16, -504.17) * mm});
            skLineSegment(sketch, "E155.bottom", {"start": v(-2379.5, -823.15) * mm, "end": v(-2165.66, -823.15) * mm});
            skLineSegment(sketch, "E155.top", {"start": v(-2379.5, -707.08) * mm, "end": v(-2165.66, -707.08) * mm});
            skLineSegment(sketch, "E155.left", {"start": v(-2379.5, -805.65) * mm, "end": v(-2379.5, -707.08) * mm});
            skLineSegment(sketch, "E155.right", {"start": v(-2165.66, -805.65) * mm, "end": v(-2165.66, -707.08) * mm});
            skLineSegment(sketch, "E156.left", {"start": v(-1956.22, -798.16) * mm, "end": v(-1956.22, -691.65) * mm});
            skArc(sketch, "E157", {"start": v(-1821.75, -691.65) * mm, "mid": v(-1888.99, -660.72) * mm, "end": v(-1956.22, -691.65) * mm});
            skLineSegment(sketch, "E158", {"start": v(-1975.05, -798.16) * mm, "end": v(-1956.22, -798.16) * mm});
            skLineSegment(sketch, "E159", {"start": v(-1975.05, -798.16) * mm, "end": v(-1975.05, -823.15) * mm});
            skLineSegment(sketch, "E160", {"start": v(-1888.99, -749.28) * mm, "end": v(-1888.99, -968.9) * mm, "construction": true});
            skLineSegment(sketch, "E161.MirrorCS", {"start": v(-1802.92, -798.16) * mm, "end": v(-1802.92, -823.15) * mm});
            skLineSegment(sketch, "E162.MirrorCS", {"start": v(-1802.92, -798.16) * mm, "end": v(-1821.75, -798.16) * mm});
            skLineSegment(sketch, "E163.trimOffspring", {"start": v(-1821.75, -798.16) * mm, "end": v(-1821.75, -691.65) * mm});
            skLineSegment(sketch, "E164.bottom", {"start": v(-2398.33, -823.15) * mm, "end": v(-2379.5, -823.15) * mm});
            skLineSegment(sketch, "E164.top", {"start": v(-2398.33, -805.65) * mm, "end": v(-2379.5, -805.65) * mm});
            skLineSegment(sketch, "E164.left", {"start": v(-2398.33, -823.15) * mm, "end": v(-2398.33, -805.65) * mm});
            skLineSegment(sketch, "E165", {"start": v(-2272.58, -707.08) * mm, "end": v(-2272.58, -783.8) * mm, "construction": true});
            skLineSegment(sketch, "E166.MirrorCS", {"start": v(-2146.83, -805.65) * mm, "end": v(-2165.66, -805.65) * mm});
            skLineSegment(sketch, "E167.MirrorCS", {"start": v(-2146.83, -823.15) * mm, "end": v(-2146.83, -805.65) * mm});
            skLineSegment(sketch, "E168", {"start": v(-1098.96, 871.24) * mm, "end": v(-1098.96, -823.15) * mm, "construction": true});
            skLineSegment(sketch, "E169", {"start": v(-1098.96, -624.56) * mm, "end": v(-1190.62, -624.56) * mm});
            skLineSegment(sketch, "E170", {"start": v(-1190.62, -624.56) * mm, "end": v(-1190.62, -771.1) * mm});
            skLineSegment(sketch, "E171", {"start": v(-1218.68, -771.1) * mm, "end": v(-1242.52, -823.15) * mm});
            skLineSegment(sketch, "E172", {"start": v(-1218.68, -771.1) * mm, "end": v(-1190.62, -771.1) * mm});
            skLineSegment(sketch, "E173.MirrorCS", {"start": v(-1098.96, -624.56) * mm, "end": v(-1007.3, -624.56) * mm});
            skLineSegment(sketch, "E174.MirrorCS", {"start": v(-1007.3, -624.56) * mm, "end": v(-1007.3, -771.1) * mm});
            skLineSegment(sketch, "E175.MirrorCS", {"start": v(-979.25, -771.1) * mm, "end": v(-1007.3, -771.1) * mm});
            skLineSegment(sketch, "E176.MirrorCS", {"start": v(-979.25, -771.1) * mm, "end": v(-955.4, -823.15) * mm});
            skPoint(sketch, "E177.start.orphan", {"position": v(-1190.62, -764.86) * mm});
            skLineSegment(sketch, "E178.bottom", {"start": v(-3039.83, 1219.82) * mm, "end": v(-2994.11, 1219.82) * mm});
            skLineSegment(sketch, "E178.top", {"start": v(-3039.83, 1171.06) * mm, "end": v(-2994.11, 1171.06) * mm});
            skLineSegment(sketch, "E178.left", {"start": v(-3039.83, 1219.82) * mm, "end": v(-3039.83, 1171.06) * mm});
            skLineSegment(sketch, "E178.right", {"start": v(-2994.11, 1219.82) * mm, "end": v(-2994.11, 1171.06) * mm});
            skLineSegment(sketch, "E179.0.1.0", {"start": v(-3039.83, 1049.82) * mm, "end": v(-2994.11, 1049.82) * mm});
            skLineSegment(sketch, "E179.0.1.1", {"start": v(-3039.83, 1049.82) * mm, "end": v(-3039.83, 1001.06) * mm});
            skLineSegment(sketch, "E179.0.1.2", {"start": v(-3039.83, 1001.06) * mm, "end": v(-2994.11, 1001.06) * mm});
            skLineSegment(sketch, "E179.0.1.3", {"start": v(-2994.11, 1049.82) * mm, "end": v(-2994.11, 1001.06) * mm});
            skLineSegment(sketch, "E179.0.2.0", {"start": v(-3039.83, 879.82) * mm, "end": v(-2994.11, 879.82) * mm});
            skLineSegment(sketch, "E179.0.2.1", {"start": v(-3039.83, 879.82) * mm, "end": v(-3039.83, 831.06) * mm});
            skLineSegment(sketch, "E179.0.2.2", {"start": v(-3039.83, 831.06) * mm, "end": v(-2994.11, 831.06) * mm});
            skLineSegment(sketch, "E179.0.2.3", {"start": v(-2994.11, 879.82) * mm, "end": v(-2994.11, 831.06) * mm});
            skLineSegment(sketch, "E179.0.3.0", {"start": v(-3039.83, 709.82) * mm, "end": v(-2994.11, 709.82) * mm});
            skLineSegment(sketch, "E179.0.3.1", {"start": v(-3039.83, 709.82) * mm, "end": v(-3039.83, 661.06) * mm});
            skLineSegment(sketch, "E179.0.3.2", {"start": v(-3039.83, 661.06) * mm, "end": v(-2994.11, 661.06) * mm});
            skLineSegment(sketch, "E179.0.3.3", {"start": v(-2994.11, 709.82) * mm, "end": v(-2994.11, 661.06) * mm});
            skLineSegment(sketch, "E179.0.4.0", {"start": v(-3039.83, 539.82) * mm, "end": v(-2994.11, 539.82) * mm});
            skLineSegment(sketch, "E179.0.4.1", {"start": v(-3039.83, 539.82) * mm, "end": v(-3039.83, 491.06) * mm});
            skLineSegment(sketch, "E179.0.4.2", {"start": v(-3039.83, 491.06) * mm, "end": v(-2994.11, 491.06) * mm});
            skLineSegment(sketch, "E179.0.4.3", {"start": v(-2994.11, 539.82) * mm, "end": v(-2994.11, 491.06) * mm});
            skLineSegment(sketch, "E179.0.5.0", {"start": v(-3039.83, 369.82) * mm, "end": v(-2994.11, 369.82) * mm});
            skLineSegment(sketch, "E179.0.5.1", {"start": v(-3039.83, 369.82) * mm, "end": v(-3039.83, 321.06) * mm});
            skLineSegment(sketch, "E179.0.5.2", {"start": v(-3039.83, 321.06) * mm, "end": v(-2994.11, 321.06) * mm});
            skLineSegment(sketch, "E179.0.5.3", {"start": v(-2994.11, 369.82) * mm, "end": v(-2994.11, 321.06) * mm});
            skLineSegment(sketch, "E179.0.6.0", {"start": v(-3039.83, 199.82) * mm, "end": v(-2994.11, 199.82) * mm});
            skLineSegment(sketch, "E179.0.6.1", {"start": v(-3039.83, 199.82) * mm, "end": v(-3039.83, 151.06) * mm});
            skLineSegment(sketch, "E179.0.6.2", {"start": v(-3039.83, 151.06) * mm, "end": v(-2994.11, 151.06) * mm});
            skLineSegment(sketch, "E179.0.6.3", {"start": v(-2994.11, 199.82) * mm, "end": v(-2994.11, 151.06) * mm});
            skLineSegment(sketch, "E179.0.7.0", {"start": v(-3039.83, 29.82) * mm, "end": v(-2994.11, 29.82) * mm});
            skLineSegment(sketch, "E179.0.7.1", {"start": v(-3039.83, 29.82) * mm, "end": v(-3039.83, -18.94) * mm});
            skLineSegment(sketch, "E179.0.7.2", {"start": v(-3039.83, -18.94) * mm, "end": v(-2994.11, -18.94) * mm});
            skLineSegment(sketch, "E179.0.7.3", {"start": v(-2994.11, 29.82) * mm, "end": v(-2994.11, -18.94) * mm});
            skLineSegment(sketch, "E179.0.9.0", {"start": v(-3039.83, -310.18) * mm, "end": v(-2994.11, -310.18) * mm});
            skLineSegment(sketch, "E179.0.9.1", {"start": v(-3039.83, -310.18) * mm, "end": v(-3039.83, -358.94) * mm});
            skLineSegment(sketch, "E179.0.9.2", {"start": v(-3039.83, -358.94) * mm, "end": v(-2994.11, -358.94) * mm});
            skLineSegment(sketch, "E179.0.9.3", {"start": v(-2994.11, -310.18) * mm, "end": v(-2994.11, -358.94) * mm});
            skLineSegment(sketch, "E179.1.0.0", {"start": v(-2949.83, 1219.82) * mm, "end": v(-2904.11, 1219.82) * mm});
            skLineSegment(sketch, "E179.1.0.1", {"start": v(-2949.83, 1219.82) * mm, "end": v(-2949.83, 1171.06) * mm});
            skLineSegment(sketch, "E179.1.0.2", {"start": v(-2949.83, 1171.06) * mm, "end": v(-2904.11, 1171.06) * mm});
            skLineSegment(sketch, "E179.1.0.3", {"start": v(-2904.11, 1219.82) * mm, "end": v(-2904.11, 1171.06) * mm});
            skLineSegment(sketch, "E179.1.1.0", {"start": v(-2949.83, 1049.82) * mm, "end": v(-2904.11, 1049.82) * mm});
            skLineSegment(sketch, "E179.1.1.1", {"start": v(-2949.83, 1049.82) * mm, "end": v(-2949.83, 1001.06) * mm});
            skLineSegment(sketch, "E179.1.1.2", {"start": v(-2949.83, 1001.06) * mm, "end": v(-2904.11, 1001.06) * mm});
            skLineSegment(sketch, "E179.1.1.3", {"start": v(-2904.11, 1049.82) * mm, "end": v(-2904.11, 1001.06) * mm});
            skLineSegment(sketch, "E179.1.2.0", {"start": v(-2949.83, 879.82) * mm, "end": v(-2904.11, 879.82) * mm});
            skLineSegment(sketch, "E179.1.2.1", {"start": v(-2949.83, 879.82) * mm, "end": v(-2949.83, 831.06) * mm});
            skLineSegment(sketch, "E179.1.2.2", {"start": v(-2949.83, 831.06) * mm, "end": v(-2904.11, 831.06) * mm});
            skLineSegment(sketch, "E179.1.2.3", {"start": v(-2904.11, 879.82) * mm, "end": v(-2904.11, 831.06) * mm});
            skLineSegment(sketch, "E179.1.3.0", {"start": v(-2949.83, 709.82) * mm, "end": v(-2904.11, 709.82) * mm});
            skLineSegment(sketch, "E179.1.3.1", {"start": v(-2949.83, 709.82) * mm, "end": v(-2949.83, 661.06) * mm});
            skLineSegment(sketch, "E179.1.3.2", {"start": v(-2949.83, 661.06) * mm, "end": v(-2904.11, 661.06) * mm});
            skLineSegment(sketch, "E179.1.3.3", {"start": v(-2904.11, 709.82) * mm, "end": v(-2904.11, 661.06) * mm});
            skLineSegment(sketch, "E179.1.4.0", {"start": v(-2949.83, 539.82) * mm, "end": v(-2904.11, 539.82) * mm});
            skLineSegment(sketch, "E179.1.4.1", {"start": v(-2949.83, 539.82) * mm, "end": v(-2949.83, 491.06) * mm});
            skLineSegment(sketch, "E179.1.4.2", {"start": v(-2949.83, 491.06) * mm, "end": v(-2904.11, 491.06) * mm});
            skLineSegment(sketch, "E179.1.4.3", {"start": v(-2904.11, 539.82) * mm, "end": v(-2904.11, 491.06) * mm});
            skLineSegment(sketch, "E179.1.5.0", {"start": v(-2949.83, 369.82) * mm, "end": v(-2904.11, 369.82) * mm});
            skLineSegment(sketch, "E179.1.5.1", {"start": v(-2949.83, 369.82) * mm, "end": v(-2949.83, 321.06) * mm});
            skLineSegment(sketch, "E179.1.5.2", {"start": v(-2949.83, 321.06) * mm, "end": v(-2904.11, 321.06) * mm});
            skLineSegment(sketch, "E179.1.5.3", {"start": v(-2904.11, 369.82) * mm, "end": v(-2904.11, 321.06) * mm});
            skLineSegment(sketch, "E179.1.7.0", {"start": v(-2949.83, 29.82) * mm, "end": v(-2904.11, 29.82) * mm});
            skLineSegment(sketch, "E179.1.7.1", {"start": v(-2949.83, 29.82) * mm, "end": v(-2949.83, -18.94) * mm});
            skLineSegment(sketch, "E179.1.7.2", {"start": v(-2949.83, -18.94) * mm, "end": v(-2904.11, -18.94) * mm});
            skLineSegment(sketch, "E179.1.7.3", {"start": v(-2904.11, 29.82) * mm, "end": v(-2904.11, -18.94) * mm});
            skLineSegment(sketch, "E179.1.8.0", {"start": v(-2949.83, -140.18) * mm, "end": v(-2904.11, -140.18) * mm});
            skLineSegment(sketch, "E179.1.8.1", {"start": v(-2949.83, -140.18) * mm, "end": v(-2949.83, -188.94) * mm});
            skLineSegment(sketch, "E179.1.8.2", {"start": v(-2949.83, -188.94) * mm, "end": v(-2904.11, -188.94) * mm});
            skLineSegment(sketch, "E179.1.8.3", {"start": v(-2904.11, -140.18) * mm, "end": v(-2904.11, -188.94) * mm});
            skLineSegment(sketch, "E179.1.9.0", {"start": v(-2949.83, -310.18) * mm, "end": v(-2904.11, -310.18) * mm});
            skLineSegment(sketch, "E179.1.9.1", {"start": v(-2949.83, -310.18) * mm, "end": v(-2949.83, -358.94) * mm});
            skLineSegment(sketch, "E179.1.9.2", {"start": v(-2949.83, -358.94) * mm, "end": v(-2904.11, -358.94) * mm});
            skLineSegment(sketch, "E179.1.9.3", {"start": v(-2904.11, -310.18) * mm, "end": v(-2904.11, -358.94) * mm});
            skLineSegment(sketch, "E179.2.2.0", {"start": v(-2859.83, 879.82) * mm, "end": v(-2814.11, 879.82) * mm});
            skLineSegment(sketch, "E179.2.2.1", {"start": v(-2859.83, 879.82) * mm, "end": v(-2859.83, 831.06) * mm});
            skLineSegment(sketch, "E179.2.2.2", {"start": v(-2859.83, 831.06) * mm, "end": v(-2814.11, 831.06) * mm});
            skLineSegment(sketch, "E179.2.2.3", {"start": v(-2814.11, 879.82) * mm, "end": v(-2814.11, 831.06) * mm});
            skLineSegment(sketch, "E179.2.3.0", {"start": v(-2859.83, 709.82) * mm, "end": v(-2814.11, 709.82) * mm});
            skLineSegment(sketch, "E179.2.3.1", {"start": v(-2859.83, 709.82) * mm, "end": v(-2859.83, 661.06) * mm});
            skLineSegment(sketch, "E179.2.3.2", {"start": v(-2859.83, 661.06) * mm, "end": v(-2814.11, 661.06) * mm});
            skLineSegment(sketch, "E179.2.3.3", {"start": v(-2814.11, 709.82) * mm, "end": v(-2814.11, 661.06) * mm});
            skLineSegment(sketch, "E179.2.5.0", {"start": v(-2859.83, 369.82) * mm, "end": v(-2814.11, 369.82) * mm});
            skLineSegment(sketch, "E179.2.5.1", {"start": v(-2859.83, 369.82) * mm, "end": v(-2859.83, 321.06) * mm});
            skLineSegment(sketch, "E179.2.5.2", {"start": v(-2859.83, 321.06) * mm, "end": v(-2814.11, 321.06) * mm});
            skLineSegment(sketch, "E179.2.5.3", {"start": v(-2814.11, 369.82) * mm, "end": v(-2814.11, 321.06) * mm});
            skLineSegment(sketch, "E179.2.6.0", {"start": v(-2859.83, 199.82) * mm, "end": v(-2814.11, 199.82) * mm});
            skLineSegment(sketch, "E179.2.6.1", {"start": v(-2859.83, 199.82) * mm, "end": v(-2859.83, 151.06) * mm});
            skLineSegment(sketch, "E179.2.6.2", {"start": v(-2859.83, 151.06) * mm, "end": v(-2814.11, 151.06) * mm});
            skLineSegment(sketch, "E179.2.6.3", {"start": v(-2814.11, 199.82) * mm, "end": v(-2814.11, 151.06) * mm});
            skLineSegment(sketch, "E179.2.7.0", {"start": v(-2859.83, 29.82) * mm, "end": v(-2814.11, 29.82) * mm});
            skLineSegment(sketch, "E179.2.7.1", {"start": v(-2859.83, 29.82) * mm, "end": v(-2859.83, -18.94) * mm});
            skLineSegment(sketch, "E179.2.7.2", {"start": v(-2859.83, -18.94) * mm, "end": v(-2814.11, -18.94) * mm});
            skLineSegment(sketch, "E179.2.7.3", {"start": v(-2814.11, 29.82) * mm, "end": v(-2814.11, -18.94) * mm});
            skLineSegment(sketch, "E179.2.8.0", {"start": v(-2859.83, -140.18) * mm, "end": v(-2814.11, -140.18) * mm});
            skLineSegment(sketch, "E179.2.8.1", {"start": v(-2859.83, -140.18) * mm, "end": v(-2859.83, -188.94) * mm});
            skLineSegment(sketch, "E179.2.8.2", {"start": v(-2859.83, -188.94) * mm, "end": v(-2814.11, -188.94) * mm});
            skLineSegment(sketch, "E179.2.8.3", {"start": v(-2814.11, -140.18) * mm, "end": v(-2814.11, -188.94) * mm});
            skLineSegment(sketch, "E179.2.9.0", {"start": v(-2859.83, -310.18) * mm, "end": v(-2814.11, -310.18) * mm});
            skLineSegment(sketch, "E179.2.9.1", {"start": v(-2859.83, -310.18) * mm, "end": v(-2859.83, -358.94) * mm});
            skLineSegment(sketch, "E179.2.9.2", {"start": v(-2859.83, -358.94) * mm, "end": v(-2814.11, -358.94) * mm});
            skLineSegment(sketch, "E179.2.9.3", {"start": v(-2814.11, -310.18) * mm, "end": v(-2814.11, -358.94) * mm});
            skLineSegment(sketch, "E179.direction1", {"start": v(-3039.83, 1171.06) * mm, "end": v(-2949.83, 1171.06) * mm, "construction": true});
            skLineSegment(sketch, "E179.direction2", {"start": v(-3039.83, 1171.06) * mm, "end": v(-3039.83, 1001.06) * mm, "construction": true});
            skPoint(sketch, "E180.orphan", {"position": v(-2814.11, 1049.82) * mm});
            skPoint(sketch, "E181.orphan", {"position": v(-2814.11, 1171.06) * mm});
            skLineSegment(sketch, "E182", {"start": v(5132.1, -547.29) * mm, "end": v(5132.1, 726.8) * mm});
            skLineSegment(sketch, "E183", {"start": v(5132.1, 726.8) * mm, "end": v(5332.19, 726.8) * mm});
            skLineSegment(sketch, "E184", {"start": v(5332.19, 726.8) * mm, "end": v(5332.76, 1173.74) * mm});
            skLineSegment(sketch, "E185", {"start": v(5332.76, 1173.74) * mm, "end": v(5506.39, 1173.74) * mm});
            skLineSegment(sketch, "E186.bottom", {"start": v(5447.94, 576.74) * mm, "end": v(5212.5, 576.74) * mm});
            skLineSegment(sketch, "E186.top", {"start": v(5322.44, 166.22) * mm, "end": v(5212.5, 166.22) * mm});
            skLineSegment(sketch, "E186.right", {"start": v(5212.5, 576.74) * mm, "end": v(5212.5, 166.22) * mm});
            skLineSegment(sketch, "E187", {"start": v(5322.21, 165.46) * mm, "end": v(5447.94, 576.74) * mm});
            skLineSegment(sketch, "E188", {"start": v(5506.39, 1173.74) * mm, "end": v(5506.39, -547.29) * mm});
            skLineSegment(sketch, "E189.bottom", {"start": v(5386.23, 144.74) * mm, "end": v(5451.4, 144.74) * mm});
            skLineSegment(sketch, "E189.top", {"start": v(5386.23, -547.29) * mm, "end": v(5451.4, -547.29) * mm});
            skLineSegment(sketch, "E189.left", {"start": v(5386.23, 144.74) * mm, "end": v(5386.23, -547.29) * mm});
            skLineSegment(sketch, "E189.right", {"start": v(5451.4, 144.74) * mm, "end": v(5451.4, -547.29) * mm});
            skLineSegment(sketch, "E190.trimOffspring", {"start": v(5506.39, -547.29) * mm, "end": v(5530, -547.29) * mm});
            skPoint(sketch, "E191.orphan", {"position": v(5332.19, 576.74) * mm});
            skLineSegment(sketch, "E192", {"start": v(5078.19, -547.29) * mm, "end": v(5132.1, -547.29) * mm});
            skSolve(sketch);
        }
        {
            var Q0;
            {var subQ3=sQuery(id+"F0.wireOp",EDGE,"E3");Q0=makeQuery(id+"F0.imprint","IMPRINT",FACE,{"disambiguationData":[TD([[makeQuery(id+"F0.imprint","IMPRINT",EDGE,{"derivedFrom":subQ3}),-1.0]])]});}
            var Q1;
            Q1=makeQuery(id+"F0.imprint","IMPRINT",FACE,{"disambiguationData":[TD([[makeQuery(id+"F0.imprint","IMPRINT",EDGE,{"derivedFrom":sQuery(id+"F0.wireOp",EDGE,"E17.right")}),1.0]])]});
            var Q2;
            {var subQ5=sQuery(id+"F0.wireOp",EDGE,"Xg3izdXC-hEsF-rlkP-HVtV-wRNKsXQCuSdC");Q2=makeQuery(id+"F0.imprint","IMPRINT",FACE,{"disambiguationData":[TD([[makeQuery(id+"F0.imprint","IMPRINT",EDGE,{"derivedFrom":subQ5}),-1.0]])]});}
            var Q3;
            {var subQ0=sQuery(id+"F0.wireOp",EDGE,"z3shH16m-4Cin-hxS3-82qS-b71axBLUNB9v");Q3=makeQuery(id+"F0.imprint","IMPRINT",FACE,{"disambiguationData":[TD([[makeQuery(id+"F0.imprint","IMPRINT",EDGE,{"derivedFrom":subQ0}),1.0]])]});}
            var Q4;
            {var subQ8=sQuery(id+"F0.wireOp",EDGE,"E24");Q4=makeQuery(id+"F0.imprint","IMPRINT",FACE,{"disambiguationData":[TD([[makeQuery(id+"F0.imprint","IMPRINT",EDGE,{"derivedFrom":subQ8}),1.0]])]});}
            var Q5;
            {var subQ0=sQuery(id+"F0.wireOp",EDGE,"jukQ9odg-WrPu-cqjV-HuHS-w9H9N4Cn54EP");Q5=makeQuery(id+"F0.imprint","IMPRINT",FACE,{"disambiguationData":[TD([[makeQuery(id+"F0.imprint","IMPRINT",EDGE,{"derivedFrom":subQ0}),1.0]])]});}
            var Q6;
            {var subQ0=sQuery(id+"F0.wireOp",EDGE,"YW6ZTAPu-my7R-QIqS-I4NO-0zTMjqCtzTD2");Q6=makeQuery(id+"F0.imprint","IMPRINT",FACE,{"disambiguationData":[TD([[makeQuery(id+"F0.imprint","IMPRINT",EDGE,{"derivedFrom":subQ0}),-1.0]])]});}
            var Q7;
            {var subQ1=sQuery(id+"F0.wireOp",EDGE,"E28");Q7=makeQuery(id+"F0.imprint","IMPRINT",FACE,{"disambiguationData":[TD([[makeQuery(id+"F0.imprint","IMPRINT",EDGE,{"derivedFrom":subQ1}),-1.0]])]});}
            var Q8;
            {var subQ1=sQuery(id+"F0.wireOp",EDGE,"2yR5sZhP-zfkW-sUfa-cihi-hqN44SL7KMfm");Q8=makeQuery(id+"F0.imprint","IMPRINT",FACE,{"disambiguationData":[TD([[makeQuery(id+"F0.imprint","IMPRINT",EDGE,{"derivedFrom":subQ1}),1.0]])]});}
            extrude(context, id + "F1", {"entities" : qUnion([Q0, Q1, Q2, Q3, Q4, Q5, Q6, Q7, Q8]), "depth" : 25.4 * mm});
        }
        {
            var Q0;
            Q0=qCreatedBy(makeId("Front.planeOp"),FACE);
            cPlane(context, id + "F2", {"entities" : qUnion([Q0]), "cplaneType" : CPlaneType.OFFSET, "offset" : 127 * mm, "oppositeDirection" : true, "width" : 152.4 * mm, "height" : 152.4 * mm});
        }
        {
            var Q0;
            Q0=qCreatedBy(id+"F2.planeOp",FACE);
            var sketch = newSketch(context, id + "F3", { "sketchPlane" : qUnion([Q0])});
            skLineSegment(sketch, "E193.bottom", {"start": v(5508.47, -850.46) * mm, "end": v(-4077.9, -850.46) * mm});
            skLineSegment(sketch, "E193.top", {"start": v(5508.47, 2253.46) * mm, "end": v(-4077.9, 2253.46) * mm});
            skLineSegment(sketch, "E193.left", {"start": v(5508.47, -850.46) * mm, "end": v(5508.47, 2253.46) * mm});
            skLineSegment(sketch, "E193.right", {"start": v(-4077.9, -850.46) * mm, "end": v(-4077.9, 2253.46) * mm});
            skLineSegment(sketch, "E194", {"start": v(-4077.9, 1084.45) * mm, "end": v(-3437, 1084.45) * mm});
            skLineSegment(sketch, "E195", {"start": v(-3437, 1084.45) * mm, "end": v(-3437, 1805.35) * mm});
            skLineSegment(sketch, "E196", {"start": v(-3437, 1805.35) * mm, "end": v(-3122.04, 1805.35) * mm});
            skLineSegment(sketch, "E197", {"start": v(-3122.04, 1805.35) * mm, "end": v(-3122.04, 1413.4) * mm});
            skLineSegment(sketch, "E198", {"start": v(-3122.04, 1413.4) * mm, "end": v(-2359.15, 1413.4) * mm});
            skLineSegment(sketch, "E199", {"start": v(-2359.15, 1413.4) * mm, "end": v(-2359.15, 2253.46) * mm});
            skLineSegment(sketch, "E200", {"start": v(-1715.24, 2253.46) * mm, "end": v(-1715.24, 1441.4) * mm});
            skLineSegment(sketch, "E201", {"start": v(-1715.24, 1441.4) * mm, "end": v(-1211.3, 1441.4) * mm});
            skLineSegment(sketch, "E202", {"start": v(-1211.3, 1441.4) * mm, "end": v(-1211.3, 2029.32) * mm});
            skLineSegment(sketch, "E203", {"start": v(-1211.3, 2029.32) * mm, "end": v(-875.35, 2029.32) * mm});
            skLineSegment(sketch, "E204", {"start": v(-875.35, 2029.32) * mm, "end": v(-875.35, 1021.46) * mm});
            skLineSegment(sketch, "E205", {"start": v(-875.35, 1021.46) * mm, "end": v(-469.4, 1021.46) * mm});
            skLineSegment(sketch, "E206", {"start": v(-469.4, 1021.46) * mm, "end": v(-469.4, 2253.46) * mm});
            skLineSegment(sketch, "E207.trimOffspring", {"start": v(-1715.24, 2253.46) * mm, "end": v(-2359.15, 2253.46) * mm});
            skSolve(sketch);
        }
        {
            var Q0;
            Q0 = qSketchRegion(id + "F3", true);
            extrude(context, id + "F4", {"entities" : qUnion([Q0]), "endBound" : BoundingType.SYMMETRIC, "depth" : 25.4 * mm});
        }
    });
